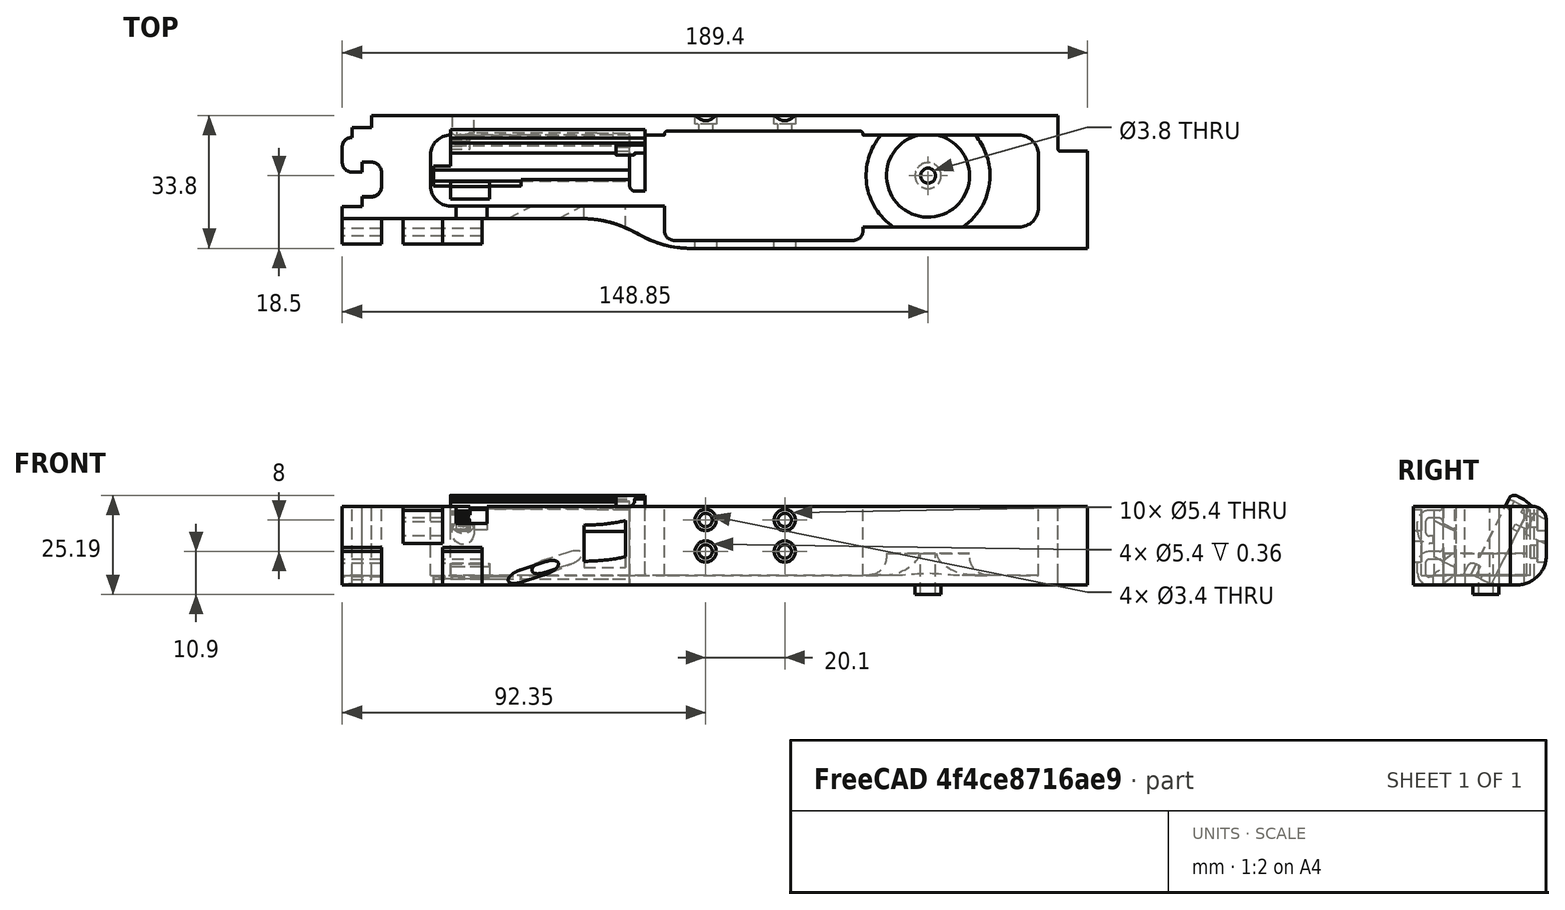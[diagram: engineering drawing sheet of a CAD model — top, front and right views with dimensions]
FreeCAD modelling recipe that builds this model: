
FCSTD DOCUMENT  (FreeCAD 0.19R0.19.2)
Label: v0_9991
License: All rights reserved
LicenseURL: http://en.wikipedia.org/wiki/All_rights_reserved
objects: Sketcher::SketchObject×44, Part::Extrusion×34, Part::MultiFuse×20, Part::Cut×15, Part::Box×14, Part::Fillet×11, App::MeasureDistance×5, Part::Cylinder×4, Part::Revolution×1, Mesh::Feature×1
note: 143 computed .brp shape members not serialized (recipe doc carries the construction recipe); baked Part::Feature solids carry a one-line shape summary decoded from their .brp

FEATURE [Sketcher::SketchObject] Sketch
  FullyConstrained = true
  sketch-geometry (36):
    g0: LineSegment StartX=0 StartY=0 StartZ=0 EndX=154.4 EndY=0 EndZ=0
    g1: LineSegment StartX=154.4 StartY=0 StartZ=0 EndX=154.4 EndY=-7.6 EndZ=0
    g2: LineSegment StartX=32.5209 StartY=-26.2 StartZ=0 EndX=-7.5 EndY=-26.2 EndZ=0
    g3-g7: Circle x5 (B-spline internal-alignment scaffolding for g8; pole/knot coordinates omitted)
    g8: BSplineCurve PolesCount=5 KnotsCount=3 Degree=3 IsPeriodic=0
    g9: GeomPoint X=61.85 Y=-33.8 Z=0
    g10: GeomPoint X=47.185 Y=-29.9 Z=0
    g11: GeomPoint X=32.5209 Y=-26.2 Z=0
    g12: Circle CenterX=121.35 CenterY=-14.3 CenterZ=0 NormalX=0 NormalY=0 NormalZ=1 AngleXU=0 Radius=3.25
    g13: LineSegment StartX=-7.5 StartY=-26.2 StartZ=0 EndX=-27.5 EndY=-26.2 EndZ=0
    g14: LineSegment StartX=-20 StartY=0 StartZ=0 EndX=0 EndY=0 EndZ=0
    g15: LineSegment StartX=-25 StartY=-3.1 StartZ=0 EndX=-20 EndY=-3.1 EndZ=0
    g16: LineSegment StartX=-25 StartY=-3.1 StartZ=0 EndX=-25 EndY=-5.6 EndZ=0
    g17: LineSegment StartX=-27.5 StartY=-8.1 StartZ=0 EndX=-27.5 EndY=-11.85 EndZ=0
    g18: ArcOfCircle CenterX=-25 CenterY=-8.1 CenterZ=0 NormalX=0 NormalY=0 NormalZ=1 AngleXU=0 Radius=2.5 StartAngle=1.5708 EndAngle=3.14159
    g19: LineSegment StartX=-25 StartY=-14.35 StartZ=0 EndX=-22.5 EndY=-14.35 EndZ=0
    g20: ArcOfCircle CenterX=-25 CenterY=-11.85 CenterZ=0 NormalX=0 NormalY=0 NormalZ=1 AngleXU=0 Radius=2.5 StartAngle=3.14159 EndAngle=4.71239
    g21: LineSegment StartX=-22.5 StartY=-14.35 StartZ=0 EndX=-22.5 EndY=-11.85 EndZ=0
    g22: LineSegment StartX=-22.5 StartY=-11.85 StartZ=0 EndX=-20 EndY=-11.85 EndZ=0
    g23: ArcOfCircle CenterX=-20 CenterY=-14.35 CenterZ=0 NormalX=0 NormalY=0 NormalZ=1 AngleXU=0 Radius=2.5 StartAngle=8e-16 EndAngle=1.5708
    g24: LineSegment StartX=-17.5 StartY=-14.35 StartZ=0 EndX=-17.5 EndY=-18.1 EndZ=0
    g25: ArcOfCircle CenterX=-20 CenterY=-18.1 CenterZ=0 NormalX=0 NormalY=0 NormalZ=1 AngleXU=0 Radius=2.5 StartAngle=4.71239 EndAngle=6.28319
    g26: LineSegment StartX=-22.5 StartY=-20.6 StartZ=0 EndX=-20 EndY=-20.6 EndZ=0
    g27: LineSegment StartX=-22.5 StartY=-20.6 StartZ=0 EndX=-22.5 EndY=-23.1 EndZ=0
    g28: LineSegment StartX=-27.5 StartY=-23.1 StartZ=0 EndX=-22.5 EndY=-23.1 EndZ=0
    g29: LineSegment StartX=-20 StartY=-3.1 StartZ=0 EndX=-20 EndY=0 EndZ=0
    g30: LineSegment StartX=-27.5 StartY=-23.1 StartZ=0 EndX=-27.5 EndY=-26.2 EndZ=0
    g31: LineSegment StartX=154.4 StartY=-7.6 StartZ=0 EndX=154.4 EndY=-8.6 EndZ=0
    g32: ArcOfCircle CenterX=154.9 CenterY=-8.6 CenterZ=0 NormalX=0 NormalY=0 NormalZ=1 AngleXU=0 Radius=0.5 StartAngle=3.14159 EndAngle=4.71239
    g33: LineSegment StartX=154.9 StartY=-9.1 StartZ=0 EndX=161.9 EndY=-9.1 EndZ=0
    g34: LineSegment StartX=161.9 StartY=-9.1 StartZ=0 EndX=161.9 EndY=-33.8 EndZ=0
    g35: LineSegment StartX=161.9 StartY=-33.8 StartZ=0 EndX=61.85 EndY=-33.8 EndZ=0
  constraints (72):
    c: PointOnObject(g0,g-2)
    c: Horizontal(g0)
    c: Distance(g0) = 154.4
    c: DistanceY(g-1,g0) = 0
    c: Vertical(g1)
    c: Distance(g1) = 7.6
    c: Coincident(g1,g0)
    c: Horizontal(g2)
    c: Block(g2)
    c: Weight(g3) = 1
    c: Coincident(g8,g2)
    c: InternalAlignment(g3-g7 -> g8) x5
    c: InternalAlignment(g9,g8)
    c: InternalAlignment(g10,g8)
    c: InternalAlignment(g11,g8)
    c: Block(g12)
    c: Coincident(g13,g2)
    c: Horizontal(g13)
    c: Distance(g13) = 20
    c: Horizontal(g14)
    c: Distance(g14) = 20
    c: Coincident(g14,g0)
    c: Horizontal(g15)
    c: Vertical(g16)
    c: Coincident(g16,g15)
    c: Vertical(g17)
    c: Coincident(g18,g16)
    c: Block(g18)
    c: Coincident(g17,g18)
    c: Horizontal(g19)
    c: Coincident(g20,g17)
    c: Block(g20)
    c: Block(g19)
    c: Vertical(g21)
    c: Coincident(g21,g19)
    c: Horizontal(g22)
    c: Coincident(g22,g21)
    c: Coincident(g23,g22)
    c: Vertical(g24)
    c: Block(g23)
    c: Coincident(g24,g23)
    c: Coincident(g25,g24)
    c: Block(g25)
    c: Horizontal(g26)
    c: Coincident(g26,g25)
    c: Vertical(g27)
    c: Coincident(g27,g26)
    c: Horizontal(g28)
    c: Coincident(g28,g27)
    c: Block(g15)
    c: Block(g28)
    c: Coincident(g29,g15)
    c: Coincident(g29,g14)
    c: Vertical(g29)
    c: Coincident(g30,g28)
    c: Coincident(g30,g13)
    c: Vertical(g30)
    c: Vertical(g31)
    c: Distance(g31) = 1
    c: Coincident(g31,g1)
    c: Coincident(g32,g31)
    c: Block(g32)
    c: Coincident(g33,g32)
    c: Horizontal(g33)
    c: Coincident(g34,g33)
    c: Vertical(g34)
    c: Block(g34)
    c: Coincident(g35,g34)
    c: Horizontal(g35)
    c: Block(g35)
    c: Coincident(g8,g35)
    c: Block(g8)
FEATURE [Part::Extrusion] Extrude  label="mainBodyBaseExtrude"
  Base = -> Sketch
  Dir = (0,0,1)
  DirMode = 2
  FaceMakerClass = Part::FaceMakerBullseye
  LengthFwd = 2.4
  LengthRev = 0
  Solid = true
  Symmetric = false
FEATURE [Sketcher::SketchObject] Sketch001
  FullyConstrained = true
  sketch-geometry (75):
    g0: ArcOfCircle CenterX=144.4 CenterY=-10 CenterZ=0 NormalX=0 NormalY=0 NormalZ=1 AngleXU=0 Radius=5 StartAngle=4.345e-13 EndAngle=1.5708
    g1: LineSegment StartX=32.5209 StartY=-26.2 StartZ=0 EndX=-7.49911 EndY=-26.2 EndZ=0
    g2: LineSegment StartX=0 StartY=0 StartZ=0 EndX=154.4 EndY=0 EndZ=0
    g3-g7: Circle x5 (B-spline internal-alignment scaffolding for g8; pole/knot coordinates omitted)
    g8: BSplineCurve PolesCount=5 KnotsCount=3 Degree=3 IsPeriodic=0
    g9: GeomPoint X=61.85 Y=-33.8 Z=0
    g10: GeomPoint X=47.1857 Y=-29.9 Z=0
    g11: GeomPoint X=32.5209 Y=-26.2 Z=0
    g12: LineSegment StartX=154.4 StartY=0 StartZ=0 EndX=154.4 EndY=-7.6 EndZ=0
    g13: LineSegment StartX=20 StartY=-5 StartZ=0 EndX=54.35 EndY=-5 EndZ=0
    g14: LineSegment StartX=104.85 StartY=-5 StartZ=0 EndX=144.4 EndY=-5 EndZ=0
    g15: LineSegment StartX=54.35 StartY=-23 StartZ=0 EndX=20 EndY=-23 EndZ=0
    g16: LineSegment StartX=-27.4991 StartY=-26.2 StartZ=0 EndX=-7.49911 EndY=-26.2 EndZ=0
    g17: LineSegment StartX=-20 StartY=0 StartZ=0 EndX=0 EndY=0 EndZ=0
    g18: LineSegment StartX=-27.4991 StartY=-23.2 StartZ=0 EndX=-22.5 EndY=-23.2 EndZ=0
    g19: LineSegment StartX=-22.5 StartY=-20.7 StartZ=0 EndX=-22.5 EndY=-23.2 EndZ=0
    g20: LineSegment StartX=-22.5 StartY=-20.7 StartZ=0 EndX=-20 EndY=-20.7 EndZ=0
    g21: ArcOfCircle CenterX=-20 CenterY=-18.2 CenterZ=0 NormalX=0 NormalY=0 NormalZ=1 AngleXU=0 Radius=2.5 StartAngle=4.71239 EndAngle=6.28319
    g22: LineSegment StartX=-17.5 StartY=-14.4 StartZ=0 EndX=-17.5 EndY=-18.2 EndZ=0
    g23: ArcOfCircle CenterX=-20 CenterY=-14.4 CenterZ=0 NormalX=0 NormalY=0 NormalZ=1 AngleXU=0 Radius=2.5 StartAngle=9e-16 EndAngle=1.5708
    g24: LineSegment StartX=-22.5 StartY=-11.9 StartZ=0 EndX=-20 EndY=-11.9 EndZ=0
    g25: LineSegment StartX=-22.5 StartY=-14.4 StartZ=0 EndX=-22.5 EndY=-11.9 EndZ=0
    g26: LineSegment StartX=-25 StartY=-14.4 StartZ=0 EndX=-22.5 EndY=-14.4 EndZ=0
    g27: ArcOfCircle CenterX=-25 CenterY=-11.9 CenterZ=0 NormalX=0 NormalY=0 NormalZ=1 AngleXU=0 Radius=2.5 StartAngle=3.14159 EndAngle=4.71239
    g28: LineSegment StartX=-27.5 StartY=-8.1 StartZ=0 EndX=-27.5 EndY=-11.9 EndZ=0
    g29: ArcOfCircle CenterX=-25 CenterY=-8.1 CenterZ=0 NormalX=0 NormalY=0 NormalZ=1 AngleXU=0 Radius=2.5 StartAngle=1.5708 EndAngle=3.14159
    g30: LineSegment StartX=-25 StartY=-3.1 StartZ=0 EndX=-25 EndY=-5.6 EndZ=0
    g31: LineSegment StartX=-20 StartY=-3.1 StartZ=0 EndX=-25 EndY=-3.1 EndZ=0
    g32: LineSegment StartX=-20 StartY=0 StartZ=0 EndX=-20 EndY=-3.1 EndZ=0
    g33: LineSegment StartX=-27.4991 StartY=-26.2 StartZ=0 EndX=-27.4991 EndY=-23.2 EndZ=0
    g34: LineSegment StartX=4.09e-14 StartY=-5 StartZ=0 EndX=20 EndY=-5 EndZ=0
    g35: ArcOfCircle CenterX=7.1e-15 CenterY=-18 CenterZ=0 NormalX=0 NormalY=0 NormalZ=1 AngleXU=0 Radius=5 StartAngle=3.14159 EndAngle=4.71239
    g36: ArcOfCircle CenterX=4.26e-14 CenterY=-10 CenterZ=0 NormalX=0 NormalY=0 NormalZ=1 AngleXU=0 Radius=5 StartAngle=1.5708 EndAngle=3.14159
    g37: LineSegment StartX=-5 StartY=-18 StartZ=0 EndX=-5 EndY=-10 EndZ=0
    g38: LineSegment StartX=6.2e-15 StartY=-23 StartZ=0 EndX=20 EndY=-23 EndZ=0
    g39: LineSegment StartX=154.4 StartY=-7.6 StartZ=0 EndX=154.4 EndY=-8.6 EndZ=0
    g40: LineSegment StartX=154.9 StartY=-9.1 StartZ=0 EndX=161.9 EndY=-9.1 EndZ=0
    g41: ArcOfCircle CenterX=154.9 CenterY=-8.6 CenterZ=0 NormalX=0 NormalY=0 NormalZ=1 AngleXU=0 Radius=0.5 StartAngle=3.14159 EndAngle=4.71299
    g42: LineSegment StartX=104.85 StartY=-28.3916 StartZ=0 EndX=144.408 EndY=-28.3916 EndZ=0
    g43: LineSegment StartX=149.4 StartY=-10 StartZ=0 EndX=149.4 EndY=-23.4 EndZ=0
    g44: ArcOfCircle CenterX=144.408 CenterY=-23.4 CenterZ=0 NormalX=0 NormalY=0 NormalZ=1 AngleXU=0 Radius=4.99164 StartAngle=4.71239 EndAngle=6.28319
    g45: LineSegment StartX=104.85 StartY=-28.3916 StartZ=0 EndX=104.85 EndY=-28.7833 EndZ=0
    g46: LineSegment StartX=54.35 StartY=-28.7916 StartZ=0 EndX=54.35 EndY=-23 EndZ=0
    g47: LineSegment StartX=161.9 StartY=-33.8 StartZ=0 EndX=161.9 EndY=-9.1 EndZ=0
    g48: LineSegment StartX=61.85 StartY=-33.8 StartZ=0 EndX=161.9 EndY=-33.8 EndZ=0
    g49: Circle CenterX=54.35 CenterY=-28.7916 CenterZ=0 NormalX=0 NormalY=0 NormalZ=1 AngleXU=0 Radius=1
    g50: Circle CenterX=54.35 CenterY=-31.7916 CenterZ=0 NormalX=0 NormalY=0 NormalZ=1 AngleXU=0 Radius=1
    g51: Circle CenterX=57.35 CenterY=-31.7916 CenterZ=0 NormalX=0 NormalY=0 NormalZ=1 AngleXU=0 Radius=1
    g52: BSplineCurve PolesCount=3 KnotsCount=2 Degree=2 IsPeriodic=0
    g53: GeomPoint X=54.35 Y=-28.7916 Z=0
    g54: GeomPoint X=57.35 Y=-31.7916 Z=0
    g55: Circle CenterX=104.85 CenterY=-28.7833 CenterZ=0 NormalX=0 NormalY=0 NormalZ=1 AngleXU=0 Radius=1
    g56: Circle CenterX=104.85 CenterY=-31.7916 CenterZ=0 NormalX=0 NormalY=0 NormalZ=1 AngleXU=0 Radius=1
    g57: Circle CenterX=101.85 CenterY=-31.7916 CenterZ=0 NormalX=0 NormalY=0 NormalZ=1 AngleXU=0 Radius=1
    g58: BSplineCurve PolesCount=3 KnotsCount=2 Degree=2 IsPeriodic=0
    g59: GeomPoint X=104.85 Y=-28.7833 Z=0
    g60: GeomPoint X=101.85 Y=-31.7916 Z=0
    g61: LineSegment StartX=57.35 StartY=-31.7916 StartZ=0 EndX=101.85 EndY=-31.7916 EndZ=0
    g62: Circle CenterX=54.35 CenterY=-5 CenterZ=0 NormalX=0 NormalY=0 NormalZ=1 AngleXU=0 Radius=1
    g63: Circle CenterX=54.35 CenterY=-4 CenterZ=0 NormalX=0 NormalY=0 NormalZ=1 AngleXU=0 Radius=1
    g64: Circle CenterX=55.15 CenterY=-4 CenterZ=0 NormalX=0 NormalY=0 NormalZ=1 AngleXU=0 Radius=1
    g65: BSplineCurve PolesCount=3 KnotsCount=2 Degree=2 IsPeriodic=0
    g66: GeomPoint X=54.35 Y=-5 Z=0
    g67: GeomPoint X=55.15 Y=-4 Z=0
    g68: Circle CenterX=104.85 CenterY=-5 CenterZ=0 NormalX=0 NormalY=0 NormalZ=1 AngleXU=0 Radius=1
    g69: Circle CenterX=104.85 CenterY=-4 CenterZ=0 NormalX=0 NormalY=0 NormalZ=1 AngleXU=0 Radius=1
    g70: Circle CenterX=104.05 CenterY=-4 CenterZ=0 NormalX=0 NormalY=0 NormalZ=1 AngleXU=0 Radius=1
    g71: BSplineCurve PolesCount=3 KnotsCount=2 Degree=2 IsPeriodic=0
    g72: GeomPoint X=104.85 Y=-5 Z=0
    g73: GeomPoint X=104.05 Y=-4 Z=0
    g74: LineSegment StartX=104.05 StartY=-4 StartZ=0 EndX=55.15 EndY=-4 EndZ=0
  constraints (156):
    c: PointOnObject(g2,g-2)
    c: DistanceY(g-1,g2) = 0
    c: Block(g0)
    c: Horizontal(g1)
    c: Distance(g1) = 40.02
    c: Horizontal(g2)
    c: Block(g2)
    c: Weight(g3) = 1
    c: Equal(g3, g4-g7) x4
    c: Coincident(g8,g1)
    c: InternalAlignment(g3-g7 -> g8) x5
    c: InternalAlignment(g9,g8)
    c: InternalAlignment(g10,g8)
    c: InternalAlignment(g11,g8)
    c: Vertical(g12)
    c: Coincident(g12,g2)
    c: Distance(g12) = 7.6
    c: Block(g12)
    c: Horizontal(g13)
    c: Coincident(g14,g0)
    c: Horizontal(g14)
    c: Horizontal(g15)
    c: Horizontal(g16)
    c: Distance(g16) = 20
    c: Coincident(g1,g16)
    c: Horizontal(g17)
    c: Distance(g17) = 20
    c: Coincident(g17,g2)
    c: Horizontal(g31)
    c: Vertical(g30)
    c: Coincident(g29,g30)
    c: Vertical(g28)
    c: Block(g29)
    c: Coincident(g27,g28)
    c: Block(g27)
    c: Horizontal(g26)
    c: Coincident(g26,g27)
    c: Vertical(g25)
    c: Coincident(g25,g26)
    c: Horizontal(g24)
    c: Coincident(g23,g24)
    c: Block(g23)
    c: Vertical(g22)
    c: Coincident(g21,g22)
    c: Block(g21)
    c: Horizontal(g20)
    c: Coincident(g20,g21)
    c: Vertical(g19)
    c: Coincident(g19,g20)
    c: Horizontal(g18)
    c: Coincident(g18,g19)
    c: Coincident(g32,g17)
    c: Coincident(g32,g31)
    c: Vertical(g32)
    c: Coincident(g33,g16)
    c: Coincident(g33,g18)
    c: Vertical(g33)
    c: Block(g33)
    c: Block(g18)
    c: Block(g22)
    c: Block(g26)
    c: Block(g25)
    c: Block(g24)
    c: Block(g28)
    c: Block(g31)
    c: Block(g30)
    c: Horizontal(g34)
    c: Distance(g34) = 20
    c: Block(g35)
    c: Block(g36)
    c: Coincident(g37,g35)
    c: Coincident(g37,g36)
    c: Vertical(g37)
    c: Coincident(g38,g35)
    c: Coincident(g38,g15)
    c: Horizontal(g38)
    c: Block(g38)
    c: Block(g34)
    c: Block(g13)
    c: Vertical(g39)
    c: Distance(g39) = 1
    c: Coincident(g39,g12)
    c: Horizontal(g40)
    c: Coincident(g41,g39)
    c: Coincident(g41,g40)
    c: Block(g39)
    c: Block(g41)
    c: Horizontal(g42)
    c: Vertical(g43)
    c: Distance(g43) = 13.4
    c: Coincident(g43,g0)
    c: Block(g42)
    c: Block(g43)
    c: Coincident(g44,g43)
    c: Coincident(g44,g42)
    c: Block(g44)
    c: Distance(g15) = 34.35
    c: Coincident(g45,g42)
    c: Vertical(g45)
    c: Coincident(g46,g15)
    c: Vertical(g46)
    c: Coincident(g47,g40)
    c: Vertical(g47)
    c: Block(g47)
    c: Coincident(g48,g47)
    c: Horizontal(g48)
    c: Block(g48)
    c: Coincident(g8,g48)
    c: Block(g8)
    c: Coincident(g52,g46)
    c: Weight(g49) = 1
    c: Equal(g49,g50)
    c: Equal(g49,g51)
    c: InternalAlignment(g49,g52)
    c: InternalAlignment(g50,g52)
    c: InternalAlignment(g51,g52)
    c: InternalAlignment(g53,g52)
    c: InternalAlignment(g54,g52)
    c: Coincident(g58,g45)
    c: Weight(g55) = 1
    c: Equal(g55,g56)
    c: Equal(g55,g57)
    c: InternalAlignment(g55,g58)
    c: InternalAlignment(g56,g58)
    c: InternalAlignment(g57,g58)
    c: InternalAlignment(g59,g58)
    c: InternalAlignment(g60,g58)
    c: Block(g58)
    c: Block(g52)
    c: Coincident(g61,g52)
    c: Coincident(g61,g58)
    c: Horizontal(g61)
    c: Block(g14)
    c: Coincident(g65,g13)
    c: Weight(g62) = 1
    c: Equal(g62,g63)
    c: Equal(g62,g64)
    c: InternalAlignment(g62,g65)
    c: InternalAlignment(g63,g65)
    c: InternalAlignment(g64,g65)
    c: InternalAlignment(g66,g65)
    c: InternalAlignment(g67,g65)
    c: Block(g65)
    c: Coincident(g71,g14)
    c: Weight(g68) = 1
    c: Equal(g68,g69)
    c: Equal(g68,g70)
    c: InternalAlignment(g68,g71)
    c: InternalAlignment(g69,g71)
    c: InternalAlignment(g70,g71)
    c: InternalAlignment(g72,g71)
    c: InternalAlignment(g73,g71)
    c: Block(g71)
    c: Coincident(g74,g71)
    c: Coincident(g74,g65)
    c: Horizontal(g74)
FEATURE [Sketcher::SketchObject] Sketch005
  FullyConstrained = true
  Placement = pos=(0,0,0) rot=(1,0,0;1.5708rad)
  sketch-geometry (4):
    g0: Circle CenterX=84.95 CenterY=16.5 CenterZ=0 NormalX=0 NormalY=0 NormalZ=1 AngleXU=0 Radius=1.7
    g1: Circle CenterX=84.95 CenterY=8.5 CenterZ=0 NormalX=0 NormalY=0 NormalZ=1 AngleXU=0 Radius=1.7
    g2: Circle CenterX=64.85 CenterY=8.5 CenterZ=0 NormalX=0 NormalY=0 NormalZ=1 AngleXU=0 Radius=1.7
    g3: Circle CenterX=64.85 CenterY=16.5 CenterZ=0 NormalX=0 NormalY=0 NormalZ=1 AngleXU=0 Radius=1.7
  constraints (4):
    c: Block(g0)
    c: Block(g1)
    c: Block(g2)
    c: Block(g3)
FEATURE [Part::Extrusion] Extrude004  label="removeFromMainBodyToCreateScrewHolesForSolenoidExtrude004"
  Base = -> Sketch005
  Dir = (0,-1,1.1e-15)
  DirMode = 2
  FaceMakerClass = Part::FaceMakerBullseye
  LengthFwd = 10
  LengthRev = 0
  Solid = true
  Symmetric = false
FEATURE [Sketcher::SketchObject] Sketch004
  FullyConstrained = true
  Placement = pos=(0,0,0) rot=(1,0,0;1.5708rad)
  sketch-geometry (12):
    g0: LineSegment StartX=15.75 StartY=2.5 StartZ=0 EndX=15.75 EndY=0 EndZ=0
    g1: Circle CenterX=15.75 CenterY=2.5 CenterZ=0 NormalX=0 NormalY=0 NormalZ=1 AngleXU=0 Radius=1
    g2: Circle CenterX=10.55 CenterY=2.5 CenterZ=0 NormalX=0 NormalY=0 NormalZ=1 AngleXU=0 Radius=1
    g3: Circle CenterX=10.55 CenterY=8 CenterZ=0 NormalX=0 NormalY=0 NormalZ=1 AngleXU=0 Radius=1
    g4: BSplineCurve PolesCount=3 KnotsCount=2 Degree=2 IsPeriodic=0
    g5: GeomPoint X=15.75 Y=2.5 Z=0
    g6: GeomPoint X=10.55 Y=8 Z=0
    g7: LineSegment StartX=1.9 StartY=8 StartZ=0 EndX=10.55 EndY=8 EndZ=0
    g8: LineSegment StartX=1.9 StartY=-2.4 StartZ=0 EndX=1.9 EndY=8 EndZ=0
    g9: LineSegment StartX=3.30092 StartY=-2.4 StartZ=0 EndX=3.30092 EndY=0 EndZ=0
    g10: LineSegment StartX=15.75 StartY=0 StartZ=0 EndX=3.30092 EndY=0 EndZ=0
    g11: LineSegment StartX=3.30092 StartY=-2.4 StartZ=0 EndX=1.9 EndY=-2.4 EndZ=0
  constraints (26):
    c: Vertical(g0)
    c: Distance(g0) = 2.5
    c: Coincident(g4,g0)
    c: Weight(g1) = 1
    c: Equal(g1,g2)
    c: Equal(g1,g3)
    c: InternalAlignment(g1,g4)
    c: InternalAlignment(g2,g4)
    c: InternalAlignment(g3,g4)
    c: InternalAlignment(g5,g4)
    c: InternalAlignment(g6,g4)
    c: Block(g4)
    c: Coincident(g7,g4)
    c: Horizontal(g7)
    c: Vertical(g8)
    c: Coincident(g8,g7)
    c: Block(g8)
    c: Vertical(g9)
    c: Coincident(g10,g0)
    c: PointOnObject(g10,g-1)
    c: Horizontal(g10)
    c: Coincident(g10,g9)
    c: Block(g9)
    c: Coincident(g11,g9)
    c: Coincident(g11,g8)
    c: Horizontal(g11)
FEATURE [Sketcher::SketchObject] Sketch007
  FullyConstrained = true
  Placement = pos=(0,-14.3,2.37) rot=(-1,0,0;2.03453rad)
  sketch-geometry (6):
    g0: LineSegment StartX=0 StartY=0 StartZ=0 EndX=45.5 EndY=0 EndZ=0
    g1: LineSegment StartX=0 StartY=0 StartZ=0 EndX=0 EndY=-21.2 EndZ=0
    g2: LineSegment StartX=45.5 StartY=0 StartZ=0 EndX=49.5 EndY=0 EndZ=0
    g3: LineSegment StartX=49.5 StartY=0 StartZ=0 EndX=49.5 EndY=-21.2 EndZ=0
    g4: LineSegment StartX=49.5 StartY=-21.2 StartZ=0 EndX=0 EndY=-21.2 EndZ=0
    g5: Circle CenterX=3.25 CenterY=-18.05 CenterZ=0 NormalX=0 NormalY=0 NormalZ=1 AngleXU=0 Radius=1.6
  constraints (15):
    c: Coincident(g0,g-1)
    c: Horizontal(g0)
    c: Distance(g0) = 45.5
    c: Coincident(g1,g0)
    c: Vertical(g1)
    c: Horizontal(g2)
    c: Distance(g2) = 4
    c: Coincident(g2,g0)
    c: Coincident(g3,g2)
    c: Vertical(g3)
    c: Block(g3)
    c: Coincident(g4,g3)
    c: Horizontal(g4)
    c: Coincident(g4,g1)
    c: Block(g5)
FEATURE [Part::Extrusion] Extrude005  label="solenoidDriverHolderExtrude005"
  Base = -> Sketch007
  Dir = (0,0.894389,-0.447291)
  DirMode = 2
  FaceMakerClass = Part::FaceMakerBullseye
  LengthFwd = 10
  LengthRev = 0
  Placement = pos=(0,0,-2) rot=(0,0,1;0rad)
  Solid = true
  Symmetric = false
FEATURE [Sketcher::SketchObject] Sketch008
  FullyConstrained = false
  Placement = pos=(0,-4.3,-2.6) rot=(-1,0,0;2.03453rad)
  sketch-geometry (1):
    g0: Circle CenterX=42.25 CenterY=-3.15 CenterZ=0 NormalX=0 NormalY=0 NormalZ=1 AngleXU=0 Radius=4.5
FEATURE [Sketcher::SketchObject] Sketch009
  FullyConstrained = true
  Placement = pos=(0,-4.3,-2.6) rot=(-1,0,0;2.03453rad)
  sketch-geometry (1):
    g0: Circle CenterX=3.25 CenterY=-18.0217 CenterZ=0 NormalX=0 NormalY=0 NormalZ=1 AngleXU=0 Radius=2.8
  constraints (1):
    c: Block(g0)
FEATURE [Sketcher::SketchObject] Sketch010
  FullyConstrained = true
  Placement = pos=(0,-14.3,2.37) rot=(-1,0,0;2.03453rad)
  sketch-geometry (1):
    g0: Circle CenterX=3.25 CenterY=-18.05 CenterZ=0 NormalX=0 NormalY=0 NormalZ=1 AngleXU=0 Radius=1.6
  constraints (1):
    c: Block(g0)
FEATURE [Part::Extrusion] Extrude008  label="removeFromScrewHole3"
  Base = -> Sketch010
  Dir = (0,0.894389,-0.447291)
  DirMode = 2
  FaceMakerClass = Part::FaceMakerBullseye
  LengthFwd = -25
  LengthRev = 0
  Placement = pos=(0,4,-4) rot=(0,0,1;0rad)
  Solid = true
  Symmetric = false
FEATURE [Sketcher::SketchObject] Sketch011
  FullyConstrained = true
  Placement = pos=(0,-14.3,2.37) rot=(-1,0,0;2.03453rad)
  sketch-geometry (4):
    g0: LineSegment StartX=49.5 StartY=-21.2 StartZ=0 EndX=49.5 EndY=-22.8 EndZ=0
    g1: LineSegment StartX=49.5 StartY=-22.8 StartZ=0 EndX=0.002238 EndY=-22.8 EndZ=0
    g2: LineSegment StartX=0.002238 StartY=-21.2 StartZ=0 EndX=0.002238 EndY=-22.8 EndZ=0
    g3: LineSegment StartX=49.5 StartY=-21.2 StartZ=0 EndX=0.002238 EndY=-21.2 EndZ=0
  constraints (10):
    c: Vertical(g0)
    c: Distance(g0) = 1.6
    c: Coincident(g1,g0)
    c: Horizontal(g1)
    c: Vertical(g2)
    c: Coincident(g2,g1)
    c: Coincident(g3,g0)
    c: Coincident(g3,g2)
    c: Horizontal(g3)
    c: Block(g3)
FEATURE [Part::Extrusion] Extrude009  label="solenoidDriverTopLipFront"
  Base = -> Sketch011
  Dir = (0,0.894389,-0.447291)
  DirMode = 2
  FaceMakerClass = Part::FaceMakerBullseye
  LengthFwd = -2
  LengthRev = 0
  Placement = pos=(0,-2.9,-0.35) rot=(0,0,1;0rad)
  Solid = true
  Symmetric = false
FEATURE [Sketcher::SketchObject] Sketch012
  FullyConstrained = true
  Placement = pos=(0,-14.3,2.37) rot=(-1,0,0;2.03453rad)
  sketch-geometry (4):
    g0: LineSegment StartX=49.5 StartY=-21.2 StartZ=0 EndX=49.5 EndY=-22.8 EndZ=0
    g1: LineSegment StartX=49.5 StartY=-22.8 StartZ=0 EndX=0.002238 EndY=-22.8 EndZ=0
    g2: LineSegment StartX=0.002238 StartY=-21.2 StartZ=0 EndX=0.002238 EndY=-22.8 EndZ=0
    g3: LineSegment StartX=49.5 StartY=-21.2 StartZ=0 EndX=0.002238 EndY=-21.2 EndZ=0
  constraints (10):
    c: Vertical(g0)
    c: Distance(g0) = 1.6
    c: Coincident(g1,g0)
    c: Horizontal(g1)
    c: Vertical(g2)
    c: Coincident(g2,g1)
    c: Coincident(g3,g0)
    c: Coincident(g3,g2)
    c: Horizontal(g3)
    c: Block(g3)
FEATURE [Part::Extrusion] Extrude010  label="solenoidDriverTopLipLowerExtrude010"
  Base = -> Sketch012
  Dir = (0,0.894389,-0.447291)
  DirMode = 2
  FaceMakerClass = Part::FaceMakerBullseye
  LengthFwd = 5.05
  LengthRev = 0
  Solid = true
  Symmetric = false
FEATURE [Sketcher::SketchObject] Sketch015
  FullyConstrained = true
  Placement = pos=(0,-14.3,2.37) rot=(-1,0,0;2.03453rad)
  sketch-geometry (4):
    g0: LineSegment StartX=0 StartY=1.5 StartZ=0 EndX=0 EndY=0 EndZ=0
    g1: LineSegment StartX=0 StartY=1.5 StartZ=0 EndX=5 EndY=1.5 EndZ=0
    g2: LineSegment StartX=5 StartY=1.5 StartZ=0 EndX=5 EndY=0 EndZ=0
    g3: LineSegment StartX=0 StartY=0 StartZ=0 EndX=5 EndY=0 EndZ=0
  constraints (13):
    c: Vertical(g0)
    c: Distance(g0) = 1.5
    c: Horizontal(g1)
    c: Distance(g1) = 5
    c: Coincident(g1,g0)
    c: Vertical(g2)
    c: Distance(g2) = 1.5
    c: Coincident(g2,g1)
    c: Block(g1)
    c: Block(g2)
    c: Block(g0)
    c: Coincident(g3,g0)
    c: Coincident(g3,g2)
FEATURE [Part::Extrusion] Extrude013  label="solenoidDriverBottomLipTopExtrude012"
  Base = -> Sketch015
  Dir = (0,0.894389,-0.447291)
  DirMode = 2
  FaceMakerClass = Part::FaceMakerBullseye
  LengthFwd = -6.5
  LengthRev = 0
  Placement = pos=(0,-14.15,19.65) rot=(1,0,0;1.5708rad)
  Solid = true
  Symmetric = false
FEATURE [Sketcher::SketchObject] Sketch016
  FullyConstrained = true
  Placement = pos=(0,0,0) rot=(1,0,0;1.5708rad)
  sketch-geometry (4):
    g0: Circle CenterX=84.15 CenterY=16.5 CenterZ=0 NormalX=0 NormalY=0 NormalZ=1 AngleXU=0 Radius=2.7
    g1: Circle CenterX=64.05 CenterY=16.5 CenterZ=0 NormalX=0 NormalY=0 NormalZ=1 AngleXU=0 Radius=2.7
    g2: Circle CenterX=64.05 CenterY=8.5 CenterZ=0 NormalX=0 NormalY=0 NormalZ=1 AngleXU=0 Radius=2.7
    g3: Circle CenterX=84.15 CenterY=8.5 CenterZ=0 NormalX=0 NormalY=0 NormalZ=1 AngleXU=0 Radius=2.7
  constraints (4):
    c: Block(g0)
    c: Block(g1)
    c: Block(g3)
    c: Block(g2)
FEATURE [Part::Extrusion] Extrude014  label="removeFromMainBodyToCreateScrewHoleCounterSinks"
  Base = -> Sketch016
  Dir = (0,-1,1.1e-15)
  DirMode = 2
  FaceMakerClass = Part::FaceMakerBullseye
  LengthFwd = 1.9
  LengthRev = 0
  Placement = pos=(0.8,-0.36,0) rot=(0,0,1;0rad)
  Solid = true
  Symmetric = false
FEATURE [Part::Extrusion] Extrude015  label="removeFromScrewHole2Extrude007"
  Base = -> Sketch009
  Dir = (0,0.894389,-0.447291)
  DirMode = 2
  FaceMakerClass = Part::FaceMakerBullseye
  LengthFwd = 10
  LengthRev = 0
  Placement = pos=(0,-8,2) rot=(0,0,1;0rad)
  Solid = true
  Symmetric = false
FEATURE [Sketcher::SketchObject] Sketch017
  FullyConstrained = true
  Placement = pos=(0,-14.3,2.37) rot=(-1,0,0;2.03453rad)
  sketch-geometry (4):
    g0: LineSegment StartX=0 StartY=1.5 StartZ=0 EndX=0 EndY=0 EndZ=0
    g1: LineSegment StartX=0 StartY=1.5 StartZ=0 EndX=5 EndY=1.5 EndZ=0
    g2: LineSegment StartX=5 StartY=1.5 StartZ=0 EndX=5 EndY=0 EndZ=0
    g3: LineSegment StartX=0 StartY=0 StartZ=0 EndX=5 EndY=0 EndZ=0
  constraints (13):
    c: Vertical(g0)
    c: Distance(g0) = 1.5
    c: Horizontal(g1)
    c: Distance(g1) = 5
    c: Coincident(g1,g0)
    c: Vertical(g2)
    c: Distance(g2) = 1.5
    c: Coincident(g2,g1)
    c: Block(g1)
    c: Block(g2)
    c: Block(g0)
    c: Coincident(g3,g0)
    c: Coincident(g3,g2)
FEATURE [Part::Extrusion] Extrude016  label="solenoidDriverBottomLipTopExtrude013"
  Base = -> Sketch017
  Dir = (0,0.894389,-0.447291)
  DirMode = 2
  FaceMakerClass = Part::FaceMakerBullseye
  LengthFwd = -6.5
  LengthRev = 0
  Placement = pos=(0,-15.45,20.3) rot=(1,0,0;1.5708rad)
  Solid = true
  Symmetric = false
FEATURE [Part::Fillet] Fillet005  label="solenoidDriverBottomLipTopFillet005"
  Base = -> Extrude016
  Edges = 1 edges r=1.4: [Edge6]
FEATURE [Sketcher::SketchObject] Sketch018
  FullyConstrained = true
  Placement = pos=(38.5,-14.3,2.37) rot=(-1,0,0;2.03453rad)
  sketch-geometry (4):
    g0: LineSegment StartX=11 StartY=0 StartZ=0 EndX=11 EndY=1.5 EndZ=0
    g1: LineSegment StartX=11 StartY=0 StartZ=0 EndX=3.6 EndY=0 EndZ=0
    g2: LineSegment StartX=3.6 StartY=0 StartZ=0 EndX=3.6 EndY=1.5 EndZ=0
    g3: LineSegment StartX=11 StartY=1.5 StartZ=0 EndX=3.6 EndY=1.5 EndZ=0
  constraints (12):
    c: PointOnObject(g0,g-1)
    c: Vertical(g0)
    c: Distance(g0) = 1.5
    c: Horizontal(g1)
    c: Distance(g1) = 7.4
    c: Coincident(g1,g0)
    c: Block(g0)
    c: Coincident(g2,g1)
    c: Vertical(g2)
    c: Coincident(g3,g0)
    c: Horizontal(g3)
    c: Coincident(g2,g3)
FEATURE [Part::Extrusion] Extrude017
  Base = -> Sketch018
  Dir = (0,0.894389,-0.447291)
  DirMode = 2
  FaceMakerClass = Part::FaceMakerBullseye
  LengthFwd = 4
  LengthRev = 0
  Placement = pos=(0,-8.212,34.025) rot=(1,0,0;1.5708rad)
  Solid = true
  Symmetric = false
FEATURE [Sketcher::SketchObject] Sketch019
  FullyConstrained = true
  Placement = pos=(0,0,0) rot=(1,0,0;1.5708rad)
  sketch-geometry (4):
    g0: Circle CenterX=84.95 CenterY=8.5 CenterZ=0 NormalX=0 NormalY=0 NormalZ=1 AngleXU=0 Radius=2.7
    g1: Circle CenterX=64.85 CenterY=8.5 CenterZ=0 NormalX=0 NormalY=0 NormalZ=1 AngleXU=0 Radius=2.7
    g2: Circle CenterX=64.85 CenterY=16.5 CenterZ=0 NormalX=0 NormalY=0 NormalZ=1 AngleXU=0 Radius=2.7
    g3: Circle CenterX=84.95 CenterY=16.5 CenterZ=0 NormalX=0 NormalY=0 NormalZ=1 AngleXU=0 Radius=2.7
  constraints (4):
    c: Block(g3)
    c: Block(g2)
    c: Block(g0)
    c: Block(g1)
FEATURE [Part::Extrusion] Extrude019  label="removeSolenoidAdjusterHoles"
  Base = -> Sketch019
  Dir = (0,-1,1.1e-15)
  DirMode = 2
  FaceMakerClass = Part::FaceMakerBullseye
  LengthFwd = 6
  LengthRev = 0
  Placement = pos=(0,-30,0) rot=(0,0,1;0rad)
  Solid = true
  Symmetric = false
FEATURE [Sketcher::SketchObject] Sketch020
  FullyConstrained = true
  Placement = pos=(0,-14.3,2.37) rot=(-1,0,0;2.03453rad)
  sketch-geometry (6):
    g0: LineSegment StartX=45.5 StartY=-21.2 StartZ=0 EndX=49.5 EndY=-21.2 EndZ=0
    g1: LineSegment StartX=45.5 StartY=0 StartZ=0 EndX=49.5 EndY=0 EndZ=0
    g2: LineSegment StartX=49.5 StartY=0 StartZ=0 EndX=49.5 EndY=-21.2 EndZ=0
    g3: LineSegment StartX=4 StartY=0 StartZ=0 EndX=4 EndY=-21.2 EndZ=0
    g4: LineSegment StartX=45.5 StartY=-21.2 StartZ=0 EndX=4 EndY=-21.2 EndZ=0
    g5: LineSegment StartX=4 StartY=0 StartZ=0 EndX=45.5 EndY=0 EndZ=0
  constraints (16):
    c: Horizontal(g0)
    c: Distance(g0) = 4
    c: Horizontal(g1)
    c: Distance(g1) = 4
    c: Coincident(g2,g1)
    c: Coincident(g2,g0)
    c: Vertical(g2)
    c: Block(g2)
    c: Vertical(g3)
    c: Coincident(g4,g0)
    c: Horizontal(g4)
    c: Coincident(g4,g3)
    c: Coincident(g5,g1)
    c: Horizontal(g5)
    c: Block(g3)
    c: Block(g5)
FEATURE [Part::Box] Box  label="Cube"
  AttacherType = Attacher::AttachEngine3D
  Height = 10
  Length = 190
  Placement = pos=(-30,0,0) rot=(0,0,1;0rad)
  Width = 10
FEATURE [Part::Fillet] Fillet008
  Base = -> Box
  Edges = 1 edges r=7.5: [Edge11]
FEATURE [Part::Box] Box001  label="Cube001"
  AttacherType = Attacher::AttachEngine3D
  Height = 10
  Length = 190
  Placement = pos=(-35,0,0) rot=(0,0,1;0rad)
  Width = 10
FEATURE [Part::Cut] Cut  label="filletMain"
  Base = -> Box001
  Placement = pos=(0,-10,0) rot=(0,0,1;0rad)
  Tool = -> Fillet008
FEATURE [Part::Box] Box002  label="Cube002"
  AttacherType = Attacher::AttachEngine3D
  Height = 30
  Length = 190
  Placement = pos=(-20,0,0) rot=(0,0,1;0rad)
  Width = 10
FEATURE [Part::Box] Box003  label="Cube003"
  AttacherType = Attacher::AttachEngine3D
  Height = 10
  Length = 190
  Placement = pos=(-90,-50,-10) rot=(0,0,1;0rad)
  Width = 50
FEATURE [Sketcher::SketchObject] Sketch021
  FullyConstrained = true
  Placement = pos=(0,-14.3,2.37) rot=(-1,0,0;2.03453rad)
  sketch-geometry (6):
    g0: LineSegment StartX=41.65 StartY=-3.15 StartZ=0 EndX=38.95 EndY=-3.15 EndZ=0
    g1: LineSegment StartX=36.25 StartY=-3.15 StartZ=0 EndX=38.95 EndY=-3.15 EndZ=0
    g2: LineSegment StartX=41.65 StartY=-3.15 StartZ=0 EndX=41.65 EndY=-7.15 EndZ=0
    g3: LineSegment StartX=38.95 StartY=-7.15 StartZ=0 EndX=41.65 EndY=-7.15 EndZ=0
    g4: LineSegment StartX=38.95 StartY=-7.15 StartZ=0 EndX=36.25 EndY=-7.15 EndZ=0
    g5: LineSegment StartX=36.25 StartY=-3.15 StartZ=0 EndX=36.25 EndY=-7.15 EndZ=0
  constraints (16):
    c: Horizontal(g0)
    c: Distance(g0) = 2.7
    c: Horizontal(g1)
    c: Distance(g1) = 2.7
    c: Coincident(g1,g0)
    c: Block(g0)
    c: Coincident(g2,g0)
    c: Vertical(g2)
    c: Horizontal(g3)
    c: Coincident(g3,g2)
    c: Horizontal(g4)
    c: Coincident(g5,g1)
    c: Vertical(g5)
    c: Coincident(g5,g4)
    c: Block(g3)
    c: Block(g4)
FEATURE [Sketcher::SketchObject] Sketch022
  FullyConstrained = true
  Placement = pos=(0,-14.3,2.37) rot=(-1,0,0;2.03453rad)
  sketch-geometry (6):
    g0: LineSegment StartX=41.65 StartY=-3.15 StartZ=0 EndX=38.95 EndY=-3.15 EndZ=0
    g1: LineSegment StartX=36.25 StartY=-3.15 StartZ=0 EndX=38.95 EndY=-3.15 EndZ=0
    g2: LineSegment StartX=41.65 StartY=-3.15 StartZ=0 EndX=41.65 EndY=-7.15 EndZ=0
    g3: LineSegment StartX=38.95 StartY=-7.15 StartZ=0 EndX=41.65 EndY=-7.15 EndZ=0
    g4: LineSegment StartX=38.95 StartY=-7.15 StartZ=0 EndX=36.25 EndY=-7.15 EndZ=0
    g5: LineSegment StartX=36.25 StartY=-3.15 StartZ=0 EndX=36.25 EndY=-7.15 EndZ=0
  constraints (16):
    c: Horizontal(g0)
    c: Distance(g0) = 2.7
    c: Horizontal(g1)
    c: Distance(g1) = 2.7
    c: Coincident(g1,g0)
    c: Block(g0)
    c: Coincident(g2,g0)
    c: Vertical(g2)
    c: Horizontal(g3)
    c: Coincident(g3,g2)
    c: Horizontal(g4)
    c: Coincident(g5,g1)
    c: Vertical(g5)
    c: Coincident(g5,g4)
    c: Block(g3)
    c: Block(g4)
FEATURE [Sketcher::SketchObject] Sketch024
  FullyConstrained = true
  Placement = pos=(0,-14.3,2.37) rot=(-1,0,0;2.03453rad)
  sketch-geometry (4):
    g0: LineSegment StartX=49.5 StartY=-21.2 StartZ=0 EndX=49.5 EndY=-22.8 EndZ=0
    g1: LineSegment StartX=49.5 StartY=-22.8 StartZ=0 EndX=0.002238 EndY=-22.8 EndZ=0
    g2: LineSegment StartX=0.002238 StartY=-21.2 StartZ=0 EndX=0.002238 EndY=-22.8 EndZ=0
    g3: LineSegment StartX=49.5 StartY=-21.2 StartZ=0 EndX=0.002238 EndY=-21.2 EndZ=0
  constraints (10):
    c: Vertical(g0)
    c: Distance(g0) = 1.6
    c: Coincident(g1,g0)
    c: Horizontal(g1)
    c: Vertical(g2)
    c: Coincident(g2,g1)
    c: Coincident(g3,g0)
    c: Coincident(g3,g2)
    c: Horizontal(g3)
    c: Block(g3)
FEATURE [Sketcher::SketchObject] Sketch025
  FullyConstrained = true
  Placement = pos=(0,-14.3,2.37) rot=(-1,0,0;2.03453rad)
  sketch-geometry (4):
    g0: LineSegment StartX=0 StartY=1.5 StartZ=0 EndX=0 EndY=0 EndZ=0
    g1: LineSegment StartX=0 StartY=1.5 StartZ=0 EndX=5 EndY=1.5 EndZ=0
    g2: LineSegment StartX=5 StartY=1.5 StartZ=0 EndX=5 EndY=0 EndZ=0
    g3: LineSegment StartX=0 StartY=0 StartZ=0 EndX=5 EndY=0 EndZ=0
  constraints (13):
    c: Vertical(g0)
    c: Distance(g0) = 1.5
    c: Horizontal(g1)
    c: Distance(g1) = 5
    c: Coincident(g1,g0)
    c: Vertical(g2)
    c: Distance(g2) = 1.5
    c: Coincident(g2,g1)
    c: Block(g1)
    c: Block(g2)
    c: Block(g0)
    c: Coincident(g3,g0)
    c: Coincident(g3,g2)
FEATURE [Part::Extrusion] Extrude022  label="solenoidDriverBottomLipTopExtrude014"
  Base = -> Sketch025
  Dir = (0,0.894389,-0.447291)
  DirMode = 2
  FaceMakerClass = Part::FaceMakerBullseye
  LengthFwd = -6.5
  LengthRev = 0
  Placement = pos=(0,-15.45,20.3) rot=(1,0,0;1.5708rad)
  Solid = true
  Symmetric = false
FEATURE [Part::Fillet] Fillet013  label="solenoidDriverBottomLipTopFillet006"
  Base = -> Extrude022
  Edges = 1 edges r=1.4: [Edge6]
  Placement = pos=(5,0,0) rot=(0,0,1;0rad)
FEATURE [Sketcher::SketchObject] Sketch026
  FullyConstrained = true
  Placement = pos=(0,-14.3,2.37) rot=(-1,0,0;2.03453rad)
  sketch-geometry (4):
    g0: LineSegment StartX=0 StartY=1.5 StartZ=0 EndX=0 EndY=0 EndZ=0
    g1: LineSegment StartX=0 StartY=1.5 StartZ=0 EndX=5 EndY=1.5 EndZ=0
    g2: LineSegment StartX=5 StartY=1.5 StartZ=0 EndX=5 EndY=0 EndZ=0
    g3: LineSegment StartX=0 StartY=0 StartZ=0 EndX=5 EndY=0 EndZ=0
  constraints (13):
    c: Vertical(g0)
    c: Distance(g0) = 1.5
    c: Horizontal(g1)
    c: Distance(g1) = 5
    c: Coincident(g1,g0)
    c: Vertical(g2)
    c: Distance(g2) = 1.5
    c: Coincident(g2,g1)
    c: Block(g1)
    c: Block(g2)
    c: Block(g0)
    c: Coincident(g3,g0)
    c: Coincident(g3,g2)
FEATURE [Part::Extrusion] Extrude023  label="solenoidDriverBottomLipTopExtrude015"
  Base = -> Sketch026
  Dir = (0,0.894389,-0.447291)
  DirMode = 2
  FaceMakerClass = Part::FaceMakerBullseye
  LengthFwd = -6.5
  LengthRev = 0
  Placement = pos=(5,-14.15,19.65) rot=(1,0,0;1.5708rad)
  Solid = true
  Symmetric = false
FEATURE [Sketcher::SketchObject] Sketch027
  FullyConstrained = true
  Placement = pos=(0,-14.3,2.37) rot=(-1,0,0;2.03453rad)
  sketch-geometry (5):
    g0: LineSegment StartX=45.5 StartY=-21.2 StartZ=0 EndX=49.5 EndY=-21.2 EndZ=0
    g1: LineSegment StartX=49.5 StartY=0 StartZ=0 EndX=49.5 EndY=-21.2 EndZ=0
    g2: LineSegment StartX=49.5 StartY=0 StartZ=0 EndX=49.5 EndY=1.6 EndZ=0
    g3: LineSegment StartX=45.5 StartY=-21.2 StartZ=0 EndX=45.5 EndY=1.6 EndZ=0
    g4: LineSegment StartX=49.5 StartY=1.6 StartZ=0 EndX=45.5 EndY=1.6 EndZ=0
  constraints (14):
    c: Horizontal(g0)
    c: Distance(g0) = 4
    c: Coincident(g1,g0)
    c: Vertical(g1)
    c: Block(g1)
    c: Vertical(g2)
    c: Distance(g2) = 1.6
    c: Block(g2)
    c: Coincident(g3,g0)
    c: Vertical(g3)
    c: Coincident(g4,g2)
    c: Horizontal(g4)
    c: Block(g0)
    c: Coincident(g3,g4)
FEATURE [Part::Extrusion] Extrude024
  Base = -> Sketch027
  Dir = (0,0.894389,-0.447291)
  DirMode = 2
  FaceMakerClass = Part::FaceMakerBullseye
  LengthFwd = 6.34
  LengthRev = 0
  Placement = pos=(0,-5.59,1) rot=(0,0,1;0rad)
  Solid = true
  Symmetric = false
FEATURE [Part::Fillet] Fillet014  label="solenoidDriverSideBarFillet014"
  Base = -> Extrude024
  Edges = 1 edges r=1.4: [Edge14]
  Placement = pos=(0,0.9,-0.45) rot=(0,0,1;0rad)
FEATURE [Part::Revolution] Revolve  label="mainScrewStandRevolve"
  Angle = 360
  Axis = (0,0,1)
  Base = (0,0,0)
  FaceMakerClass = Part::FaceMakerBullseye
  Placement = pos=(121.35,-15.3,0) rot=(0,0,1;0rad)
  Solid = true
  Source = -> Sketch004
  Symmetric = false
FEATURE [Part::Extrusion] Extrude021  label="solenoidDriverTopLipLowerExtrude011"
  Base = -> Sketch024
  Dir = (0,0.894389,-0.447291)
  DirMode = 2
  FaceMakerClass = Part::FaceMakerBullseye
  LengthFwd = 5.05
  LengthRev = 0
  Solid = true
  Symmetric = false
FEATURE [Part::Fillet] Fillet012  label="solenoidDriverTopLipLowerFillet004"
  Base = -> Extrude021
  Edges = 1 edges r=1.2: [Edge7]
  Placement = pos=(0,-0.9,-1.35) rot=(0,0,1;0rad)
FEATURE [Part::Fillet] Fillet003  label="solenoidDriverTopLipLowerFillet003"
  Base = -> Extrude010
  Edges = 1 edges r=1.2: [Edge7]
  Placement = pos=(0,-3,-0.3) rot=(0,0,1;0rad)
FEATURE [Part::Extrusion] Extrude025  label="mainBodyUpperExtrude025"
  Base = -> Sketch001
  Dir = (0,0,1)
  DirMode = 2
  FaceMakerClass = Part::FaceMakerBullseye
  LengthFwd = 20
  LengthRev = 0
  Solid = true
  Symmetric = false
FEATURE [Part::MultiFuse] Fusion  label="solenoidDriverBottomLipFusion"
  Placement = pos=(0,-1.6,0) rot=(0,0,1;0rad)
  Shapes = -> [Fillet005,Fillet013,Extrude023,Extrude013]
FEATURE [Sketcher::SketchObject] Sketch028
  FullyConstrained = true
  Placement = pos=(0,-14.3,2.37) rot=(-1,0,0;2.03453rad)
  sketch-geometry (4):
    g0: LineSegment StartX=0 StartY=1.5 StartZ=0 EndX=0 EndY=0 EndZ=0
    g1: LineSegment StartX=0 StartY=1.5 StartZ=0 EndX=5 EndY=1.5 EndZ=0
    g2: LineSegment StartX=5 StartY=1.5 StartZ=0 EndX=5 EndY=0 EndZ=0
    g3: LineSegment StartX=0 StartY=0 StartZ=0 EndX=5 EndY=0 EndZ=0
  constraints (13):
    c: Vertical(g0)
    c: Distance(g0) = 1.5
    c: Horizontal(g1)
    c: Distance(g1) = 5
    c: Coincident(g1,g0)
    c: Vertical(g2)
    c: Distance(g2) = 1.5
    c: Coincident(g2,g1)
    c: Block(g1)
    c: Block(g2)
    c: Block(g0)
    c: Coincident(g3,g0)
    c: Coincident(g3,g2)
FEATURE [Part::Extrusion] Extrude026  label="solenoidDriverBottomLipTopExtrude016"
  Base = -> Sketch028
  Dir = (0,0.894389,-0.447291)
  DirMode = 2
  FaceMakerClass = Part::FaceMakerBullseye
  LengthFwd = -6.5
  LengthRev = 0
  Placement = pos=(5,-14.15,19.65) rot=(1,0,0;1.5708rad)
  Solid = true
  Symmetric = false
FEATURE [Sketcher::SketchObject] Sketch029
  FullyConstrained = true
  Placement = pos=(0,-14.3,2.37) rot=(-1,0,0;2.03453rad)
  sketch-geometry (4):
    g0: LineSegment StartX=0 StartY=1.5 StartZ=0 EndX=0 EndY=0 EndZ=0
    g1: LineSegment StartX=0 StartY=1.5 StartZ=0 EndX=5 EndY=1.5 EndZ=0
    g2: LineSegment StartX=5 StartY=1.5 StartZ=0 EndX=5 EndY=0 EndZ=0
    g3: LineSegment StartX=0 StartY=0 StartZ=0 EndX=5 EndY=0 EndZ=0
  constraints (13):
    c: Vertical(g0)
    c: Distance(g0) = 1.5
    c: Horizontal(g1)
    c: Distance(g1) = 5
    c: Coincident(g1,g0)
    c: Vertical(g2)
    c: Distance(g2) = 1.5
    c: Coincident(g2,g1)
    c: Block(g1)
    c: Block(g2)
    c: Block(g0)
    c: Coincident(g3,g0)
    c: Coincident(g3,g2)
FEATURE [Part::Extrusion] Extrude027  label="solenoidDriverBottomLipTopExtrude017"
  Base = -> Sketch029
  Dir = (0,0.894389,-0.447291)
  DirMode = 2
  FaceMakerClass = Part::FaceMakerBullseye
  LengthFwd = -6.5
  LengthRev = 0
  Placement = pos=(0,-14.15,19.65) rot=(1,0,0;1.5708rad)
  Solid = true
  Symmetric = false
FEATURE [Sketcher::SketchObject] Sketch030
  FullyConstrained = true
  Placement = pos=(0,-14.3,2.37) rot=(-1,0,0;2.03453rad)
  sketch-geometry (4):
    g0: LineSegment StartX=0 StartY=1.5 StartZ=0 EndX=0 EndY=0 EndZ=0
    g1: LineSegment StartX=0 StartY=1.5 StartZ=0 EndX=5 EndY=1.5 EndZ=0
    g2: LineSegment StartX=5 StartY=1.5 StartZ=0 EndX=5 EndY=0 EndZ=0
    g3: LineSegment StartX=0 StartY=0 StartZ=0 EndX=5 EndY=0 EndZ=0
  constraints (13):
    c: Vertical(g0)
    c: Distance(g0) = 1.5
    c: Horizontal(g1)
    c: Distance(g1) = 5
    c: Coincident(g1,g0)
    c: Vertical(g2)
    c: Distance(g2) = 1.5
    c: Coincident(g2,g1)
    c: Block(g1)
    c: Block(g2)
    c: Block(g0)
    c: Coincident(g3,g0)
    c: Coincident(g3,g2)
FEATURE [Sketcher::SketchObject] Sketch031
  FullyConstrained = true
  Placement = pos=(0,-14.3,2.37) rot=(-1,0,0;2.03453rad)
  sketch-geometry (6):
    g0: LineSegment StartX=45.5 StartY=-21.2 StartZ=0 EndX=49.5 EndY=-21.2 EndZ=0
    g1: LineSegment StartX=45.5 StartY=0 StartZ=0 EndX=49.5 EndY=0 EndZ=0
    g2: LineSegment StartX=49.5 StartY=0 StartZ=0 EndX=49.5 EndY=-21.2 EndZ=0
    g3: LineSegment StartX=4 StartY=0 StartZ=0 EndX=4 EndY=-21.2 EndZ=0
    g4: LineSegment StartX=45.5 StartY=-21.2 StartZ=0 EndX=4 EndY=-21.2 EndZ=0
    g5: LineSegment StartX=4 StartY=0 StartZ=0 EndX=45.5 EndY=0 EndZ=0
  constraints (16):
    c: Horizontal(g0)
    c: Distance(g0) = 4
    c: Horizontal(g1)
    c: Distance(g1) = 4
    c: Coincident(g2,g1)
    c: Coincident(g2,g0)
    c: Vertical(g2)
    c: Block(g2)
    c: Vertical(g3)
    c: Coincident(g4,g0)
    c: Horizontal(g4)
    c: Coincident(g4,g3)
    c: Coincident(g5,g1)
    c: Horizontal(g5)
    c: Block(g3)
    c: Block(g5)
FEATURE [Part::Extrusion] Extrude028  label="removeFromSolenoidDriverMainExtrude021"
  Base = -> Sketch031
  Dir = (0,0.894389,-0.447291)
  DirMode = 2
  FaceMakerClass = Part::FaceMakerBullseye
  LengthFwd = 3.1
  LengthRev = 0
  Placement = pos=(-4,-2.42,-0.8) rot=(0,0,1;0rad)
  Solid = true
  Symmetric = false
FEATURE [Part::Extrusion] Extrude029  label="solenoidDriverBottomLipTopExtrude018"
  Base = -> Sketch030
  Dir = (0,0.894389,-0.447291)
  DirMode = 2
  FaceMakerClass = Part::FaceMakerBullseye
  LengthFwd = -6.5
  LengthRev = 0
  Placement = pos=(5,-14.15,19.65) rot=(1,0,0;1.5708rad)
  Solid = true
  Symmetric = false
FEATURE [Sketcher::SketchObject] Sketch032
  FullyConstrained = true
  Placement = pos=(0,-14.3,2.37) rot=(-1,0,0;2.03453rad)
  sketch-geometry (4):
    g0: LineSegment StartX=0 StartY=1.5 StartZ=0 EndX=0 EndY=0 EndZ=0
    g1: LineSegment StartX=0 StartY=1.5 StartZ=0 EndX=5 EndY=1.5 EndZ=0
    g2: LineSegment StartX=5 StartY=1.5 StartZ=0 EndX=5 EndY=0 EndZ=0
    g3: LineSegment StartX=0 StartY=0 StartZ=0 EndX=5 EndY=0 EndZ=0
  constraints (13):
    c: Vertical(g0)
    c: Distance(g0) = 1.5
    c: Horizontal(g1)
    c: Distance(g1) = 5
    c: Coincident(g1,g0)
    c: Vertical(g2)
    c: Distance(g2) = 1.5
    c: Coincident(g2,g1)
    c: Block(g1)
    c: Block(g2)
    c: Block(g0)
    c: Coincident(g3,g0)
    c: Coincident(g3,g2)
FEATURE [Part::Extrusion] Extrude030  label="solenoidDriverBottomLipTopExtrude019"
  Base = -> Sketch032
  Dir = (0,0.894389,-0.447291)
  DirMode = 2
  FaceMakerClass = Part::FaceMakerBullseye
  LengthFwd = -6.5
  LengthRev = 0
  Placement = pos=(0,-14.15,19.65) rot=(1,0,0;1.5708rad)
  Solid = true
  Symmetric = false
FEATURE [Part::MultiFuse] Fusion004
  Placement = pos=(0,1.4,2.65) rot=(0,0,1;0rad)
  Shapes = -> [Extrude029,Extrude030]
FEATURE [Part::MultiFuse] Fusion003
  Placement = pos=(-2.3,0,0) rot=(0,0,1;0rad)
  Shapes = -> [Extrude028,Fusion004]
FEATURE [Sketcher::SketchObject] Sketch033
  FullyConstrained = true
  Placement = pos=(0,-14.3,2.37) rot=(-1,0,0;2.03453rad)
  sketch-geometry (4):
    g0: LineSegment StartX=0 StartY=1.5 StartZ=0 EndX=0 EndY=0 EndZ=0
    g1: LineSegment StartX=0 StartY=1.5 StartZ=0 EndX=5 EndY=1.5 EndZ=0
    g2: LineSegment StartX=5 StartY=1.5 StartZ=0 EndX=5 EndY=0 EndZ=0
    g3: LineSegment StartX=0 StartY=0 StartZ=0 EndX=5 EndY=0 EndZ=0
  constraints (13):
    c: Vertical(g0)
    c: Distance(g0) = 1.5
    c: Horizontal(g1)
    c: Distance(g1) = 5
    c: Coincident(g1,g0)
    c: Vertical(g2)
    c: Distance(g2) = 1.5
    c: Coincident(g2,g1)
    c: Block(g1)
    c: Block(g2)
    c: Block(g0)
    c: Coincident(g3,g0)
    c: Coincident(g3,g2)
FEATURE [Sketcher::SketchObject] Sketch034
  FullyConstrained = true
  Placement = pos=(0,-14.3,2.37) rot=(-1,0,0;2.03453rad)
  sketch-geometry (4):
    g0: LineSegment StartX=0 StartY=1.5 StartZ=0 EndX=0 EndY=0 EndZ=0
    g1: LineSegment StartX=0 StartY=1.5 StartZ=0 EndX=5 EndY=1.5 EndZ=0
    g2: LineSegment StartX=5 StartY=1.5 StartZ=0 EndX=5 EndY=0 EndZ=0
    g3: LineSegment StartX=0 StartY=0 StartZ=0 EndX=5 EndY=0 EndZ=0
  constraints (13):
    c: Vertical(g0)
    c: Distance(g0) = 1.5
    c: Horizontal(g1)
    c: Distance(g1) = 5
    c: Coincident(g1,g0)
    c: Vertical(g2)
    c: Distance(g2) = 1.5
    c: Coincident(g2,g1)
    c: Block(g1)
    c: Block(g2)
    c: Block(g0)
    c: Coincident(g3,g0)
    c: Coincident(g3,g2)
FEATURE [Part::Extrusion] Extrude020  label="removeFromSolenoidDriverMainExtrude020"
  Base = -> Sketch020
  Dir = (0,0.894389,-0.447291)
  DirMode = 2
  FaceMakerClass = Part::FaceMakerBullseye
  LengthFwd = 3.1
  LengthRev = 0
  Placement = pos=(-4,-2.42,-0.8) rot=(0,0,1;0rad)
  Solid = true
  Symmetric = false
FEATURE [Part::Fillet] Fillet
  Base = -> Fusion003
  Edges = 1 edges r=10: [Edge5]
  Placement = pos=(-2,0,0) rot=(0,0,1;0rad)
FEATURE [Part::MultiFuse] Fusion001
  Placement = pos=(0,1.4,2.65) rot=(0,0,1;0rad)
  Shapes = -> [Extrude026,Extrude027]
FEATURE [Part::MultiFuse] Fusion002
  Shapes = -> [Extrude020,Fusion001]
FEATURE [Sketcher::SketchObject] Sketch035
  FullyConstrained = true
  Placement = pos=(0,-14.3,2.37) rot=(-1,0,0;2.03453rad)
  sketch-geometry (4):
    g0: LineSegment StartX=0 StartY=1.5 StartZ=0 EndX=0 EndY=0 EndZ=0
    g1: LineSegment StartX=0 StartY=1.5 StartZ=0 EndX=5 EndY=1.5 EndZ=0
    g2: LineSegment StartX=5 StartY=1.5 StartZ=0 EndX=5 EndY=0 EndZ=0
    g3: LineSegment StartX=0 StartY=0 StartZ=0 EndX=5 EndY=0 EndZ=0
  constraints (13):
    c: Vertical(g0)
    c: Distance(g0) = 1.5
    c: Horizontal(g1)
    c: Distance(g1) = 5
    c: Coincident(g1,g0)
    c: Vertical(g2)
    c: Distance(g2) = 1.5
    c: Coincident(g2,g1)
    c: Block(g1)
    c: Block(g2)
    c: Block(g0)
    c: Coincident(g3,g0)
    c: Coincident(g3,g2)
FEATURE [Sketcher::SketchObject] Sketch036
  FullyConstrained = true
  Placement = pos=(0,-14.3,2.37) rot=(-1,0,0;2.03453rad)
  sketch-geometry (4):
    g0: LineSegment StartX=0 StartY=1.5 StartZ=0 EndX=0 EndY=0 EndZ=0
    g1: LineSegment StartX=0 StartY=1.5 StartZ=0 EndX=5 EndY=1.5 EndZ=0
    g2: LineSegment StartX=5 StartY=1.5 StartZ=0 EndX=5 EndY=0 EndZ=0
    g3: LineSegment StartX=0 StartY=0 StartZ=0 EndX=5 EndY=0 EndZ=0
  constraints (13):
    c: Vertical(g0)
    c: Distance(g0) = 1.5
    c: Horizontal(g1)
    c: Distance(g1) = 5
    c: Coincident(g1,g0)
    c: Vertical(g2)
    c: Distance(g2) = 1.5
    c: Coincident(g2,g1)
    c: Block(g1)
    c: Block(g2)
    c: Block(g0)
    c: Coincident(g3,g0)
    c: Coincident(g3,g2)
FEATURE [Part::Extrusion] Extrude031  label="solenoidDriverBottomLipTopExtrude020"
  Base = -> Sketch035
  Dir = (0,0.894389,-0.447291)
  DirMode = 2
  FaceMakerClass = Part::FaceMakerBullseye
  LengthFwd = -6.5
  LengthRev = 0
  Placement = pos=(5,-14.15,19.65) rot=(1,0,0;1.5708rad)
  Solid = true
  Symmetric = false
FEATURE [Part::Extrusion] Extrude032  label="solenoidDriverBottomLipTopExtrude021"
  Base = -> Sketch036
  Dir = (0,0.894389,-0.447291)
  DirMode = 2
  FaceMakerClass = Part::FaceMakerBullseye
  LengthFwd = -6.5
  LengthRev = 0
  Placement = pos=(0,-14.15,19.65) rot=(1,0,0;1.5708rad)
  Solid = true
  Symmetric = false
FEATURE [Part::MultiFuse] Fusion009
  Placement = pos=(8,1.4,2.65) rot=(0,0,1;0rad)
  Shapes = -> [Extrude031,Extrude032]
FEATURE [Part::MultiFuse] Fusion010  label="removeFromSolenoidDriver"
  Shapes = -> [Fusion009,Fillet,Fusion002]
FEATURE [Sketcher::SketchObject] Sketch037
  FullyConstrained = true
  Placement = pos=(0,0,0) rot=(1,0,0;1.5708rad)
  sketch-geometry (4):
    g0: Circle CenterX=64.05 CenterY=16.5 CenterZ=0 NormalX=0 NormalY=0 NormalZ=1 AngleXU=0 Radius=2.7
    g1: Circle CenterX=64.05 CenterY=8.5 CenterZ=0 NormalX=0 NormalY=0 NormalZ=1 AngleXU=0 Radius=2.7
    g2: Circle CenterX=84.15 CenterY=8.5 CenterZ=0 NormalX=0 NormalY=0 NormalZ=1 AngleXU=0 Radius=2.7
    g3: Circle CenterX=84.15 CenterY=16.5 CenterZ=0 NormalX=0 NormalY=0 NormalZ=1 AngleXU=0 Radius=2.7
  constraints (4):
    c: Block(g2)
    c: Block(g3)
    c: Block(g0)
    c: Block(g1)
FEATURE [Part::Extrusion] Extrude033  label="removeFromMainBodyToCreateScrewHoleCounterSinks001"
  Base = -> Sketch037
  Dir = (0,-1,1.1e-15)
  DirMode = 2
  FaceMakerClass = Part::FaceMakerBullseye
  LengthFwd = 1.9
  LengthRev = 0
  Placement = pos=(0.8,0,0) rot=(0,0,1;0rad)
  Solid = true
  Symmetric = false
FEATURE [Part::MultiFuse] Fusion011  label="removeFromMainBodyToCreateScrewHoleCounterSinks001Fusion011"
  Shapes = -> [Extrude014,Extrude033]
FEATURE [Sketcher::SketchObject] Sketch038
  FullyConstrained = true
  Placement = pos=(0,-14.3,2.37) rot=(-1,0,0;2.03453rad)
  sketch-geometry (4):
    g0: LineSegment StartX=33.9 StartY=-9.7 StartZ=0 EndX=33.9 EndY=-1.5 EndZ=0
    g1: LineSegment StartX=33.9 StartY=-1.5 StartZ=0 EndX=44.5 EndY=-1.5 EndZ=0
    g2: LineSegment StartX=33.9 StartY=-9.7 StartZ=0 EndX=44.5 EndY=-9.7 EndZ=0
    g3: LineSegment StartX=44.5 StartY=-1.5 StartZ=0 EndX=44.5 EndY=-9.7 EndZ=0
  constraints (10):
    c: Vertical(g0)
    c: Coincident(g1,g0)
    c: Horizontal(g1)
    c: Block(g1)
    c: Block(g0)
    c: Coincident(g2,g0)
    c: Horizontal(g2)
    c: Coincident(g3,g1)
    c: Coincident(g3,g2)
    c: Vertical(g3)
FEATURE [Part::Extrusion] Extrude034
  Base = -> Sketch038
  Dir = (0,0.894389,-0.447291)
  DirMode = 2
  FaceMakerClass = Part::FaceMakerBullseye
  LengthFwd = 16
  LengthRev = 0
  Placement = pos=(0,-22,7) rot=(0,0,1;0rad)
  Solid = true
  Symmetric = false
FEATURE [Sketcher::SketchObject] Sketch039
  FullyConstrained = true
  Placement = pos=(0,-14.3,2.37) rot=(-1,0,0;2.03453rad)
  sketch-geometry (4):
    g0: LineSegment StartX=5.5 StartY=-7.7 StartZ=0 EndX=13.3 EndY=-7.7 EndZ=0
    g1: LineSegment StartX=13.3 StartY=-7.7 StartZ=0 EndX=13.3 EndY=-13.1 EndZ=0
    g2: LineSegment StartX=13.3 StartY=-13.1 StartZ=0 EndX=5.5 EndY=-13.1 EndZ=0
    g3: LineSegment StartX=5.5 StartY=-7.7 StartZ=0 EndX=5.5 EndY=-13.1 EndZ=0
  constraints (12):
    c: Horizontal(g0)
    c: Distance(g0) = 7.8
    c: Coincident(g1,g0)
    c: Vertical(g1)
    c: Distance(g1) = 5.4
    c: Coincident(g2,g1)
    c: Horizontal(g2)
    c: Vertical(g3)
    c: Coincident(g3,g2)
    c: Block(g0)
    c: Block(g2)
    c: Block(g3)
FEATURE [Part::Extrusion] Extrude035  label="removeToMakeHoleForConnectorExtrude035"
  Base = -> Sketch039
  Dir = (0,0.894389,-0.447291)
  DirMode = 2
  FaceMakerClass = Part::FaceMakerBullseye
  LengthFwd = 15
  LengthRev = 0
  Placement = pos=(-4,-22,9.6469) rot=(0,0,1;0rad)
  Solid = true
  Symmetric = false
FEATURE [App::MeasureDistance] Distance  label="Distance: 4.00 mm"
  Distance = 4.00184
  P1 = (119.349,-15.3,8)
  P2 = (123.351,-15.3,8)
FEATURE [App::MeasureDistance] Distance001  label="Distance: 3.80 mm"
  Distance = 3.8
  P1 = (119.45,-15.3,8)
  P2 = (123.25,-15.3,8)
FEATURE [Part::Fillet] Fillet015
  Base = -> Extrude009
  Edges = 1 edges r=1.59: [Edge7]
FEATURE [Part::Fillet] Fillet016
  Base = -> Extrude017
  Edges = 1 edges r=1.49: [Edge12]
FEATURE [Part::Fillet] Fillet017
  Base = -> Fillet016
  Edges = 1 edges r=1.45: [Edge8]
FEATURE [Part::MultiFuse] Fusion012  label="main"
  Shapes = -> [Extrude,Revolve,Extrude005,Fillet003,Fillet012,Fillet014,Extrude025,Fusion,Fillet015,Fillet017]
FEATURE [Part::Cut] Cut001
  Base = -> Fusion012
  Tool = -> Box003
FEATURE [Part::Cut] Cut002
  Base = -> Cut001
  Tool = -> Box002
FEATURE [Part::Cut] Cut003
  Base = -> Cut002
  Tool = -> Cut
FEATURE [Part::Cut] Cut004
  Base = -> Cut003
  Tool = -> Extrude019
FEATURE [Part::Cut] Cut005
  Base = -> Cut004
  Tool = -> Fusion011
FEATURE [Part::Cut] Cut006
  Base = -> Cut005
  Tool = -> Extrude004
FEATURE [Part::Cut] Cut007
  Base = -> Cut006
  Tool = -> Extrude015
FEATURE [Part::Cut] Cut008
  Base = -> Cut007
  Tool = -> Extrude008
FEATURE [Part::Cut] Cut009
  Base = -> Cut008
  Tool = -> Fusion010
FEATURE [App::MeasureDistance] Distance002  label="Distance: 2.05 mm"
  Distance = 2.05453
  P1 = (1.5,-23.0732,21.402)
  P2 = (6e-15,-23,20)
FEATURE [Part::Cut] Cut010
  Base = -> Cut009
  Tool = -> Extrude035
FEATURE [Part::Cut] Cut011
  Base = -> Cut010
  Tool = -> Extrude034
FEATURE [Part::Box] Box004  label="Cube004"
  AttacherType = Attacher::AttachEngine3D
  Height = 10
  Length = 200
  Placement = pos=(-30,0,0) rot=(0,0,1;0rad)
  Width = 10
FEATURE [Part::Fillet] Fillet020
  Base = -> Box004
  Edges = 1 edges r=3.6: [Edge12]
FEATURE [Part::Box] Box005  label="Cube005"
  AttacherType = Attacher::AttachEngine3D
  Height = 10
  Length = 198
  Placement = pos=(-30,0,0) rot=(0,0,1;0rad)
  Width = 10
FEATURE [Part::Cut] Cut012
  Base = -> Box005
  Tool = -> Fillet020
FEATURE [Part::Box] Box006  label="Cube006"
  AttacherType = Attacher::AttachEngine3D
  Height = 5
  Length = 200
  Placement = pos=(-30,6.4,10) rot=(1,0,0;0rad)
  Width = 5
FEATURE [Part::Box] Box007  label="Cube007"
  AttacherType = Attacher::AttachEngine3D
  Height = 5
  Length = 200
  Placement = pos=(-30,6.4,10) rot=(1,0,0;0.872665rad)
  Width = 5
FEATURE [Part::MultiFuse] Fusion013  label="removeFromMainFusion013"
  Placement = pos=(0,-10,10) rot=(0,0,1;0rad)
  Shapes = -> [Box007,Box006,Cut012]
FEATURE [Mesh::Feature] v0_98_Cut013  label="v0_98-Cut013"
FEATURE [App::MeasureDistance] Distance003  label="Distance: 7.18 mm"
  Distance = 7.17719
  P1 = (117.773,-15.3145,-2.4)
  P2 = (124.951,-15.2973,-2.4)
FEATURE [Sketcher::SketchObject] Sketch040
  FullyConstrained = true
  Placement = pos=(0,-14.3,2.37) rot=(-1,0,0;2.03453rad)
  sketch-geometry (4):
    g0: LineSegment StartX=0 StartY=1.5 StartZ=0 EndX=0 EndY=0 EndZ=0
    g1: LineSegment StartX=0 StartY=1.5 StartZ=0 EndX=5 EndY=1.5 EndZ=0
    g2: LineSegment StartX=5 StartY=1.5 StartZ=0 EndX=5 EndY=0 EndZ=0
    g3: LineSegment StartX=0 StartY=0 StartZ=0 EndX=5 EndY=0 EndZ=0
  constraints (13):
    c: Vertical(g0)
    c: Distance(g0) = 1.5
    c: Horizontal(g1)
    c: Distance(g1) = 5
    c: Coincident(g1,g0)
    c: Vertical(g2)
    c: Distance(g2) = 1.5
    c: Coincident(g2,g1)
    c: Block(g1)
    c: Block(g2)
    c: Block(g0)
    c: Coincident(g3,g0)
    c: Coincident(g3,g2)
FEATURE [Part::Extrusion] Extrude036
  Base = -> Sketch040
  Dir = (0,0.894389,-0.447291)
  DirMode = 2
  FaceMakerClass = Part::FaceMakerBullseye
  LengthFwd = 1.4
  LengthRev = 0
  Placement = pos=(0,8.25,17.58) rot=(0,0,1;0rad)
  Solid = true
  Symmetric = false
FEATURE [Sketcher::SketchObject] Sketch041
  FullyConstrained = true
  Placement = pos=(0,-14.3,2.37) rot=(-1,0,0;2.03453rad)
  sketch-geometry (4):
    g0: LineSegment StartX=0 StartY=1.5 StartZ=0 EndX=0 EndY=0 EndZ=0
    g1: LineSegment StartX=0 StartY=1.5 StartZ=0 EndX=5 EndY=1.5 EndZ=0
    g2: LineSegment StartX=5 StartY=1.5 StartZ=0 EndX=5 EndY=0 EndZ=0
    g3: LineSegment StartX=0 StartY=0 StartZ=0 EndX=5 EndY=0 EndZ=0
  constraints (13):
    c: Vertical(g0)
    c: Distance(g0) = 1.5
    c: Horizontal(g1)
    c: Distance(g1) = 5
    c: Coincident(g1,g0)
    c: Vertical(g2)
    c: Distance(g2) = 1.5
    c: Coincident(g2,g1)
    c: Block(g1)
    c: Block(g2)
    c: Block(g0)
    c: Coincident(g3,g0)
    c: Coincident(g3,g2)
FEATURE [Part::Extrusion] Extrude037
  Base = -> Sketch041
  Dir = (0,0.894389,-0.447291)
  DirMode = 2
  FaceMakerClass = Part::FaceMakerBullseye
  LengthFwd = 1.4
  LengthRev = 0
  Placement = pos=(0,6.11,13.33) rot=(0,0,1;0rad)
  Solid = true
  Symmetric = false
FEATURE [Part::MultiFuse] Fusion014  label="screwSpacerFusion014"
  Shapes = -> [Extrude037,Extrude036]
FEATURE [Sketcher::SketchObject] Sketch042
  FullyConstrained = true
  Placement = pos=(0,-14.3,2.37) rot=(-1,0,0;2.03453rad)
  sketch-geometry (4):
    g0: LineSegment StartX=0 StartY=1.5 StartZ=0 EndX=0 EndY=0 EndZ=0
    g1: LineSegment StartX=0 StartY=1.5 StartZ=0 EndX=5 EndY=1.5 EndZ=0
    g2: LineSegment StartX=5 StartY=1.5 StartZ=0 EndX=5 EndY=0 EndZ=0
    g3: LineSegment StartX=0 StartY=0 StartZ=0 EndX=5 EndY=0 EndZ=0
  constraints (13):
    c: Vertical(g0)
    c: Distance(g0) = 1.5
    c: Horizontal(g1)
    c: Distance(g1) = 5
    c: Coincident(g1,g0)
    c: Vertical(g2)
    c: Distance(g2) = 1.5
    c: Coincident(g2,g1)
    c: Block(g1)
    c: Block(g2)
    c: Block(g0)
    c: Coincident(g3,g0)
    c: Coincident(g3,g2)
FEATURE [Part::Extrusion] Extrude038
  Base = -> Sketch042
  Dir = (0,0.894389,-0.447291)
  DirMode = 2
  FaceMakerClass = Part::FaceMakerBullseye
  LengthFwd = 1.4
  LengthRev = 0
  Placement = pos=(0,8.459,18) rot=(0,0,1;0rad)
  Solid = true
  Symmetric = false
FEATURE [Part::MultiFuse] Fusion015  label="screwSpacerFusion014Fusion015"
  Placement = pos=(0,0.35,-0.18) rot=(0,0,1;0rad)
  Shapes = -> [Extrude038,Fusion014]
FEATURE [Part::Cylinder] Cylinder
  Angle = 360
  AttacherType = Attacher::AttachEngine3D
  Height = 10
  Placement = pos=(0,10,0) rot=(0,0,1;0rad)
  Radius = 1.5
FEATURE [Part::Cylinder] Cylinder001
  Angle = 360
  AttacherType = Attacher::AttachEngine3D
  Height = 10
  Placement = pos=(3,10,0) rot=(0,0,1;0rad)
  Radius = 1.5
FEATURE [Part::Box] Box008  label="Cube008"
  AttacherType = Attacher::AttachEngine3D
  Height = 10
  Length = 3
  Placement = pos=(0,8.5,0) rot=(0,0,1;0rad)
  Width = 3
FEATURE [Part::MultiFuse] Fusion016  label="holeForWireFusion016"
  Shapes = -> [Cylinder001,Box008,Cylinder]
FEATURE [Part::Box] Box009  label="Cube009"
  AttacherType = Attacher::AttachEngine3D
  Height = 10
  Length = 3
  Placement = pos=(0,8.5,0) rot=(0,0,1;0rad)
  Width = 3
FEATURE [Part::Cylinder] Cylinder002
  Angle = 360
  AttacherType = Attacher::AttachEngine3D
  Height = 10
  Placement = pos=(0,10,0) rot=(0,0,1;0rad)
  Radius = 1.5
FEATURE [Part::Cylinder] Cylinder003
  Angle = 360
  AttacherType = Attacher::AttachEngine3D
  Height = 10
  Placement = pos=(3,10,0) rot=(0,0,1;0rad)
  Radius = 1.5
FEATURE [Part::MultiFuse] Fusion017  label="holeForWireFusion017"
  Placement = pos=(0,0,10) rot=(0,0,1;0rad)
  Shapes = -> [Cylinder003,Box009,Cylinder002]
FEATURE [Part::MultiFuse] Fusion018  label="holeForWireFusion018"
  Placement = pos=(0,0,0) rot=(0,1,0;-1.5708rad)
  Shapes = -> [Fusion017,Fusion016]
FEATURE [Part::Box] Box010  label="Cube010"
  AttacherType = Attacher::AttachEngine3D
  Height = 0.1
  Length = 0.1
  Placement = pos=(-2,10,0) rot=(0,0.995037,0.099504;0rad)
  Width = 0.1
FEATURE [Part::MultiFuse] Fusion019
  Placement = pos=(0,10,0) rot=(1,0,0;1.5708rad)
  Shapes = -> [Box010,Fusion018]
FEATURE [Part::Box] Box011  label="Cube011"
  AttacherType = Attacher::AttachEngine3D
  Height = 0.1
  Length = 1.1
  Placement = pos=(-2,10,10) rot=(0,0.995037,0.099504;0rad)
  Width = 0.1
FEATURE [Part::MultiFuse] Fusion020
  Placement = pos=(0,0,0) rot=(0,1,0;0.349066rad)
  Shapes = -> [Box011,Fusion019]
FEATURE [Part::Box] Box012  label="Cube012"
  AttacherType = Attacher::AttachEngine3D
  Height = 0.1
  Length = 1.1
  Placement = pos=(-2,10,10) rot=(0,0.995037,0.099504;0rad)
  Width = 0.1
FEATURE [Part::MultiFuse] Fusion021
  Placement = pos=(0,30,0) rot=(0,0,1;-2.6529rad)
  Shapes = -> [Box012,Fusion020]
FEATURE [Part::Box] Box013  label="Cube013"
  AttacherType = Attacher::AttachEngine3D
  Height = 0.1
  Length = 1.1
  Placement = pos=(2,19,10) rot=(0,0.995037,0.099504;0rad)
  Width = 0.1
FEATURE [Part::MultiFuse] Fusion022  label="holeForWire"
  Placement = pos=(15,-49.8,-8.2) rot=(0,0,1;0rad)
  Shapes = -> [Box013,Fusion021]
FEATURE [Part::Cut] Cut013
  Base = -> Cut011
  Tool = -> Fusion013
FEATURE [Part::Cut] Cut014
  Base = -> Cut013
  Tool = -> Fusion022
FEATURE [Sketcher::SketchObject] Sketch043
  FullyConstrained = true
  MapMode = 4
  Placement = pos=(0,0,0) rot=(0.57735,0.57735,0.57735;2.0944rad)
  Support = -> [Cut014]
  sketch-geometry (14):
    g0: LineSegment StartX=6.08745 StartY=-4.11588 StartZ=0 EndX=6.08745 EndY=-2.11589 EndZ=0
    g1: LineSegment StartX=3.58745 StartY=2.38411 StartZ=0 EndX=3.58745 EndY=4.38411 EndZ=0
    g2: LineSegment StartX=8.08745 StartY=1.38411 StartZ=0 EndX=8.08745 EndY=-1.11589 EndZ=0
    g3: ArcOfCircle CenterX=7.08745 CenterY=-1.11589 CenterZ=0 NormalX=0 NormalY=0 NormalZ=1 AngleXU=0 Radius=1 StartAngle=4.71239 EndAngle=6.28319
    g4: LineSegment StartX=6.08745 StartY=-2.11589 StartZ=0 EndX=7.08745 EndY=-2.11589 EndZ=0
    g5: LineSegment StartX=6.08745 StartY=-4.11588 StartZ=0 EndX=7.08745 EndY=-4.11588 EndZ=0
    g6: ArcOfCircle CenterX=7.08745 CenterY=-1.11589 CenterZ=0 NormalX=0 NormalY=0 NormalZ=1 AngleXU=0 Radius=3 StartAngle=4.71239 EndAngle=6.28319
    g7: ArcOfCircle CenterX=7.08745 CenterY=1.38411 CenterZ=0 NormalX=0 NormalY=0 NormalZ=1 AngleXU=0 Radius=1 StartAngle=5.35e-14 EndAngle=1.5708
    g8: LineSegment StartX=3.58745 StartY=4.38411 StartZ=0 EndX=7.08745 EndY=4.38411 EndZ=0
    g9: LineSegment StartX=10.0875 StartY=-1.11588 StartZ=0 EndX=10.0875 EndY=1.38411 EndZ=0
    g10: ArcOfCircle CenterX=7.08745 CenterY=1.38411 CenterZ=0 NormalX=0 NormalY=0 NormalZ=1 AngleXU=0 Radius=3 StartAngle=3.57e-14 EndAngle=1.5708
    g11: LineSegment StartX=3.58745 StartY=2.38411 StartZ=0 EndX=3.58745 EndY=1.38411 EndZ=0
    g12: ArcOfCircle CenterX=4.58745 CenterY=1.38412 CenterZ=0 NormalX=0 NormalY=0 NormalZ=1 AngleXU=0 Radius=1 StartAngle=1.57081 EndAngle=3.14159
    g13: LineSegment StartX=4.58744 StartY=2.38411 StartZ=0 EndX=7.08745 EndY=2.38411 EndZ=0
  constraints (33):
    c: Vertical(g0)
    c: Vertical(g1)
    c: Distance(g1) = 2
    c: Block(g0)
    c: Block(g2)
    c: Coincident(g3,g2)
    c: Coincident(g4,g0)
    c: Coincident(g4,g3)
    c: Horizontal(g4)
    c: Block(g3)
    c: Coincident(g5,g0)
    c: Horizontal(g5)
    c: Coincident(g6,g3)
    c: Block(g6)
    c: Block(g5)
    c: Coincident(g7,g2)
    c: Block(g7)
    c: Coincident(g8,g1)
    c: Coincident(g9,g6)
    c: Vertical(g9)
    c: Coincident(g10,g7)
    c: Block(g10)
    c: Block(g8)
    c: Block(g9)
    c: Coincident(g11,g1)
    c: Vertical(g11)
    c: Distance(g11) = 1
    c: Coincident(g12,g11)
    c: Coincident(g13,g12)
    c: Coincident(g13,g7)
    c: Horizontal(g13)
    c: Block(g13)
    c: Block(g12)
FEATURE [Sketcher::SketchObject] Sketch044
  FullyConstrained = true
  MapMode = 4
  Placement = pos=(0,0,0) rot=(0.57735,0.57735,0.57735;2.0944rad)
  Support = -> [Cut014]
  sketch-geometry (14):
    g0: LineSegment StartX=6.08745 StartY=-4.11588 StartZ=0 EndX=6.08745 EndY=-2.11589 EndZ=0
    g1: LineSegment StartX=8.08745 StartY=1.38411 StartZ=0 EndX=8.08745 EndY=-1.11589 EndZ=0
    g2: ArcOfCircle CenterX=7.08745 CenterY=-1.11589 CenterZ=0 NormalX=0 NormalY=0 NormalZ=1 AngleXU=0 Radius=1 StartAngle=4.71239 EndAngle=6.28319
    g3: LineSegment StartX=6.08745 StartY=-2.11589 StartZ=0 EndX=7.08745 EndY=-2.11589 EndZ=0
    g4: LineSegment StartX=6.08745 StartY=-4.11588 StartZ=0 EndX=7.08745 EndY=-4.11588 EndZ=0
    g5: ArcOfCircle CenterX=7.08745 CenterY=-1.11589 CenterZ=0 NormalX=0 NormalY=0 NormalZ=1 AngleXU=0 Radius=3 StartAngle=4.71239 EndAngle=6.28319
    g6: ArcOfCircle CenterX=7.08745 CenterY=1.38411 CenterZ=0 NormalX=0 NormalY=0 NormalZ=1 AngleXU=0 Radius=1 StartAngle=5.35e-14 EndAngle=1.5708
    g7: LineSegment StartX=10.0875 StartY=-1.11588 StartZ=0 EndX=10.0875 EndY=1.38411 EndZ=0
    g8: ArcOfCircle CenterX=7.08745 CenterY=1.38411 CenterZ=0 NormalX=0 NormalY=0 NormalZ=1 AngleXU=0 Radius=3 StartAngle=3.57e-14 EndAngle=1.5708
    g9: ArcOfCircle CenterX=4.58745 CenterY=1.38412 CenterZ=0 NormalX=0 NormalY=0 NormalZ=1 AngleXU=0 Radius=1 StartAngle=1.57081 EndAngle=3.14159
    g10: LineSegment StartX=4.58744 StartY=2.38411 StartZ=0 EndX=7.08745 EndY=2.38411 EndZ=0
    g11: LineSegment StartX=4.58745 StartY=4.38411 StartZ=0 EndX=7.08745 EndY=4.38411 EndZ=0
    g12: ArcOfCircle CenterX=4.58745 CenterY=5.38411 CenterZ=0 NormalX=0 NormalY=0 NormalZ=1 AngleXU=0 Radius=1 StartAngle=3.14159 EndAngle=4.71239
    g13: LineSegment StartX=3.58745 StartY=5.38411 StartZ=0 EndX=3.58745 EndY=1.38411 EndZ=0
  constraints (33):
    c: Vertical(g0)
    c: Block(g0)
    c: Block(g1)
    c: Coincident(g2,g1)
    c: Coincident(g3,g0)
    c: Coincident(g3,g2)
    c: Horizontal(g3)
    c: Block(g2)
    c: Coincident(g4,g0)
    c: Horizontal(g4)
    c: Coincident(g5,g2)
    c: Block(g5)
    c: Block(g4)
    c: Coincident(g6,g1)
    c: Block(g6)
    c: Coincident(g7,g5)
    c: Vertical(g7)
    c: Coincident(g8,g6)
    c: Block(g8)
    c: Block(g7)
    c: Coincident(g10,g9)
    c: Coincident(g10,g6)
    c: Horizontal(g10)
    c: Block(g10)
    c: Block(g9)
    c: Coincident(g11,g8)
    c: Horizontal(g11)
    c: Block(g12)
    c: Block(g11)
    c: Coincident(g13,g12)
    c: Coincident(g13,g9)
    c: Vertical(g13)
    c: Tangent(g13,g9)
FEATURE [Part::Extrusion] Extrude039
  Base = -> Sketch044
  Dir = (1,0,0)
  DirMode = 2
  FaceMakerClass = Part::FaceMakerBullseye
  LengthFwd = 10
  LengthRev = 0
  Placement = pos=(8,-22.615,4.115) rot=(0,0,1;3.14159rad)
  Solid = true
  Symmetric = false
FEATURE [App::MeasureDistance] Distance004  label="Distance: 42.16 mm"
  Distance = 42.1607
  P1 = (14.6786,-26.2,1.24491)
  P2 = (-27.4815,-26.2,1.03853)
FEATURE [Sketcher::SketchObject] Sketch045
  FullyConstrained = true
  MapMode = 4
  Placement = pos=(0,0,0) rot=(0.57735,0.57735,0.57735;2.0944rad)
  Support = -> [Cut014]
  sketch-geometry (14):
    g0: LineSegment StartX=6.08745 StartY=-4.11588 StartZ=0 EndX=6.08745 EndY=-2.11589 EndZ=0
    g1: LineSegment StartX=8.08745 StartY=1.38411 StartZ=0 EndX=8.08745 EndY=-1.11589 EndZ=0
    g2: ArcOfCircle CenterX=7.08745 CenterY=-1.11589 CenterZ=0 NormalX=0 NormalY=0 NormalZ=1 AngleXU=0 Radius=1 StartAngle=4.71239 EndAngle=6.28319
    g3: LineSegment StartX=6.08745 StartY=-2.11589 StartZ=0 EndX=7.08745 EndY=-2.11589 EndZ=0
    g4: LineSegment StartX=6.08745 StartY=-4.11588 StartZ=0 EndX=7.08745 EndY=-4.11588 EndZ=0
    g5: ArcOfCircle CenterX=7.08745 CenterY=-1.11589 CenterZ=0 NormalX=0 NormalY=0 NormalZ=1 AngleXU=0 Radius=3 StartAngle=4.71239 EndAngle=6.28319
    g6: ArcOfCircle CenterX=7.08745 CenterY=1.38411 CenterZ=0 NormalX=0 NormalY=0 NormalZ=1 AngleXU=0 Radius=1 StartAngle=5.35e-14 EndAngle=1.5708
    g7: LineSegment StartX=10.0875 StartY=-1.11588 StartZ=0 EndX=10.0875 EndY=1.38411 EndZ=0
    g8: ArcOfCircle CenterX=7.08745 CenterY=1.38411 CenterZ=0 NormalX=0 NormalY=0 NormalZ=1 AngleXU=0 Radius=3 StartAngle=3.57e-14 EndAngle=1.5708
    g9: ArcOfCircle CenterX=4.58745 CenterY=1.38412 CenterZ=0 NormalX=0 NormalY=0 NormalZ=1 AngleXU=0 Radius=1 StartAngle=1.57081 EndAngle=3.14159
    g10: LineSegment StartX=4.58744 StartY=2.38411 StartZ=0 EndX=7.08745 EndY=2.38411 EndZ=0
    g11: LineSegment StartX=4.58745 StartY=4.38411 StartZ=0 EndX=7.08745 EndY=4.38411 EndZ=0
    g12: ArcOfCircle CenterX=4.58745 CenterY=5.38411 CenterZ=0 NormalX=0 NormalY=0 NormalZ=1 AngleXU=0 Radius=1 StartAngle=3.14159 EndAngle=4.71239
    g13: LineSegment StartX=3.58745 StartY=5.38411 StartZ=0 EndX=3.58745 EndY=1.38411 EndZ=0
  constraints (33):
    c: Vertical(g0)
    c: Block(g0)
    c: Block(g1)
    c: Coincident(g2,g1)
    c: Coincident(g3,g0)
    c: Coincident(g3,g2)
    c: Horizontal(g3)
    c: Block(g2)
    c: Coincident(g4,g0)
    c: Horizontal(g4)
    c: Coincident(g5,g2)
    c: Block(g5)
    c: Block(g4)
    c: Coincident(g6,g1)
    c: Block(g6)
    c: Coincident(g7,g5)
    c: Vertical(g7)
    c: Coincident(g8,g6)
    c: Block(g8)
    c: Block(g7)
    c: Coincident(g10,g9)
    c: Coincident(g10,g6)
    c: Horizontal(g10)
    c: Block(g10)
    c: Block(g9)
    c: Coincident(g11,g8)
    c: Horizontal(g11)
    c: Block(g12)
    c: Block(g11)
    c: Coincident(g13,g12)
    c: Coincident(g13,g9)
    c: Vertical(g13)
    c: Tangent(g13,g9)
FEATURE [Part::Extrusion] Extrude040
  Base = -> Sketch045
  Dir = (1,0,0)
  DirMode = 2
  FaceMakerClass = Part::FaceMakerBullseye
  LengthFwd = 10
  LengthRev = 0
  Placement = pos=(-17.5,-22.615,4.115) rot=(0,0,1;3.14159rad)
  Solid = true
  Symmetric = false
FEATURE [Sketcher::SketchObject] Sketch046
  FullyConstrained = true
  MapMode = 4
  Placement = pos=(0,0,0) rot=(0.57735,0.57735,0.57735;2.0944rad)
  Support = -> [Cut014]
  sketch-geometry (14):
    g0: LineSegment StartX=6.08745 StartY=-4.11588 StartZ=0 EndX=6.08745 EndY=-2.11589 EndZ=0
    g1: LineSegment StartX=8.08745 StartY=1.38411 StartZ=0 EndX=8.08745 EndY=-1.11589 EndZ=0
    g2: ArcOfCircle CenterX=7.08745 CenterY=-1.11589 CenterZ=0 NormalX=0 NormalY=0 NormalZ=1 AngleXU=0 Radius=1 StartAngle=4.71239 EndAngle=6.28319
    g3: LineSegment StartX=6.08745 StartY=-2.11589 StartZ=0 EndX=7.08745 EndY=-2.11589 EndZ=0
    g4: LineSegment StartX=6.08745 StartY=-4.11588 StartZ=0 EndX=7.08745 EndY=-4.11588 EndZ=0
    g5: ArcOfCircle CenterX=7.08745 CenterY=-1.11589 CenterZ=0 NormalX=0 NormalY=0 NormalZ=1 AngleXU=0 Radius=3 StartAngle=4.71239 EndAngle=6.28319
    g6: ArcOfCircle CenterX=7.08745 CenterY=1.38411 CenterZ=0 NormalX=0 NormalY=0 NormalZ=1 AngleXU=0 Radius=1 StartAngle=5.35e-14 EndAngle=1.5708
    g7: LineSegment StartX=10.0875 StartY=-1.11588 StartZ=0 EndX=10.0875 EndY=1.38411 EndZ=0
    g8: ArcOfCircle CenterX=7.08745 CenterY=1.38411 CenterZ=0 NormalX=0 NormalY=0 NormalZ=1 AngleXU=0 Radius=3 StartAngle=3.57e-14 EndAngle=1.5708
    g9: ArcOfCircle CenterX=4.58745 CenterY=1.38412 CenterZ=0 NormalX=0 NormalY=0 NormalZ=1 AngleXU=0 Radius=1 StartAngle=1.57081 EndAngle=3.14159
    g10: LineSegment StartX=4.58744 StartY=2.38411 StartZ=0 EndX=7.08745 EndY=2.38411 EndZ=0
    g11: LineSegment StartX=4.58745 StartY=4.38411 StartZ=0 EndX=7.08745 EndY=4.38411 EndZ=0
    g12: ArcOfCircle CenterX=4.58745 CenterY=5.38411 CenterZ=0 NormalX=0 NormalY=0 NormalZ=1 AngleXU=0 Radius=1 StartAngle=3.14159 EndAngle=4.71239
    g13: LineSegment StartX=3.58745 StartY=5.38411 StartZ=0 EndX=3.58745 EndY=1.38411 EndZ=0
  constraints (33):
    c: Vertical(g0)
    c: Block(g0)
    c: Block(g1)
    c: Coincident(g2,g1)
    c: Coincident(g3,g0)
    c: Coincident(g3,g2)
    c: Horizontal(g3)
    c: Block(g2)
    c: Coincident(g4,g0)
    c: Horizontal(g4)
    c: Coincident(g5,g2)
    c: Block(g5)
    c: Block(g4)
    c: Coincident(g6,g1)
    c: Block(g6)
    c: Coincident(g7,g5)
    c: Vertical(g7)
    c: Coincident(g8,g6)
    c: Block(g8)
    c: Block(g7)
    c: Coincident(g10,g9)
    c: Coincident(g10,g6)
    c: Horizontal(g10)
    c: Block(g10)
    c: Block(g9)
    c: Coincident(g11,g8)
    c: Horizontal(g11)
    c: Block(g12)
    c: Block(g11)
    c: Coincident(g13,g12)
    c: Coincident(g13,g9)
    c: Vertical(g13)
    c: Tangent(g13,g9)
FEATURE [Sketcher::SketchObject] Sketch047
  FullyConstrained = true
  MapMode = 4
  Placement = pos=(0,0,0) rot=(0.57735,0.57735,0.57735;2.0944rad)
  Support = -> [Cut014]
  sketch-geometry (14):
    g0: LineSegment StartX=6.08745 StartY=-4.11588 StartZ=0 EndX=6.08745 EndY=-2.11589 EndZ=0
    g1: LineSegment StartX=8.08745 StartY=1.38411 StartZ=0 EndX=8.08745 EndY=-1.11589 EndZ=0
    g2: ArcOfCircle CenterX=7.08745 CenterY=-1.11589 CenterZ=0 NormalX=0 NormalY=0 NormalZ=1 AngleXU=0 Radius=1 StartAngle=4.71239 EndAngle=6.28319
    g3: LineSegment StartX=6.08745 StartY=-2.11589 StartZ=0 EndX=7.08745 EndY=-2.11589 EndZ=0
    g4: LineSegment StartX=6.08745 StartY=-4.11588 StartZ=0 EndX=7.08745 EndY=-4.11588 EndZ=0
    g5: ArcOfCircle CenterX=7.08745 CenterY=-1.11589 CenterZ=0 NormalX=0 NormalY=0 NormalZ=1 AngleXU=0 Radius=3 StartAngle=4.71239 EndAngle=6.28319
    g6: ArcOfCircle CenterX=7.08745 CenterY=1.38411 CenterZ=0 NormalX=0 NormalY=0 NormalZ=1 AngleXU=0 Radius=1 StartAngle=5.35e-14 EndAngle=1.5708
    g7: LineSegment StartX=10.0875 StartY=-1.11588 StartZ=0 EndX=10.0875 EndY=1.38411 EndZ=0
    g8: ArcOfCircle CenterX=7.08745 CenterY=1.38411 CenterZ=0 NormalX=0 NormalY=0 NormalZ=1 AngleXU=0 Radius=3 StartAngle=3.57e-14 EndAngle=1.5708
    g9: ArcOfCircle CenterX=4.58745 CenterY=1.38412 CenterZ=0 NormalX=0 NormalY=0 NormalZ=1 AngleXU=0 Radius=1 StartAngle=1.57081 EndAngle=3.14159
    g10: LineSegment StartX=4.58744 StartY=2.38411 StartZ=0 EndX=7.08745 EndY=2.38411 EndZ=0
    g11: LineSegment StartX=4.58745 StartY=4.38411 StartZ=0 EndX=7.08745 EndY=4.38411 EndZ=0
    g12: ArcOfCircle CenterX=4.58745 CenterY=5.38411 CenterZ=0 NormalX=0 NormalY=0 NormalZ=1 AngleXU=0 Radius=1 StartAngle=3.14159 EndAngle=4.71239
    g13: LineSegment StartX=3.58745 StartY=5.38411 StartZ=0 EndX=3.58745 EndY=1.38411 EndZ=0
  constraints (33):
    c: Vertical(g0)
    c: Block(g0)
    c: Block(g1)
    c: Coincident(g2,g1)
    c: Coincident(g3,g0)
    c: Coincident(g3,g2)
    c: Horizontal(g3)
    c: Block(g2)
    c: Coincident(g4,g0)
    c: Horizontal(g4)
    c: Coincident(g5,g2)
    c: Block(g5)
    c: Block(g4)
    c: Coincident(g6,g1)
    c: Block(g6)
    c: Coincident(g7,g5)
    c: Vertical(g7)
    c: Coincident(g8,g6)
    c: Block(g8)
    c: Block(g7)
    c: Coincident(g10,g9)
    c: Coincident(g10,g6)
    c: Horizontal(g10)
    c: Block(g10)
    c: Block(g9)
    c: Coincident(g11,g8)
    c: Horizontal(g11)
    c: Block(g12)
    c: Block(g11)
    c: Coincident(g13,g12)
    c: Coincident(g13,g9)
    c: Vertical(g13)
    c: Tangent(g13,g9)
FEATURE [Sketcher::SketchObject] Sketch048
  FullyConstrained = true
  MapMode = 4
  Placement = pos=(0,0,0) rot=(0.57735,0.57735,0.57735;2.0944rad)
  Support = -> [Cut014]
  sketch-geometry (14):
    g0: LineSegment StartX=6.08745 StartY=-4.11588 StartZ=0 EndX=6.08745 EndY=-2.11589 EndZ=0
    g1: LineSegment StartX=8.08745 StartY=1.38411 StartZ=0 EndX=8.08745 EndY=-1.11589 EndZ=0
    g2: ArcOfCircle CenterX=7.08745 CenterY=-1.11589 CenterZ=0 NormalX=0 NormalY=0 NormalZ=1 AngleXU=0 Radius=1 StartAngle=4.71239 EndAngle=6.28319
    g3: LineSegment StartX=6.08745 StartY=-2.11589 StartZ=0 EndX=7.08745 EndY=-2.11589 EndZ=0
    g4: LineSegment StartX=6.08745 StartY=-4.11588 StartZ=0 EndX=7.08745 EndY=-4.11588 EndZ=0
    g5: ArcOfCircle CenterX=7.08745 CenterY=-1.11589 CenterZ=0 NormalX=0 NormalY=0 NormalZ=1 AngleXU=0 Radius=3 StartAngle=4.71239 EndAngle=6.28319
    g6: ArcOfCircle CenterX=7.08745 CenterY=1.38411 CenterZ=0 NormalX=0 NormalY=0 NormalZ=1 AngleXU=0 Radius=1 StartAngle=5.35e-14 EndAngle=1.5708
    g7: LineSegment StartX=10.0875 StartY=-1.11588 StartZ=0 EndX=10.0875 EndY=1.38411 EndZ=0
    g8: ArcOfCircle CenterX=7.08745 CenterY=1.38411 CenterZ=0 NormalX=0 NormalY=0 NormalZ=1 AngleXU=0 Radius=3 StartAngle=3.57e-14 EndAngle=1.5708
    g9: ArcOfCircle CenterX=4.58745 CenterY=1.38412 CenterZ=0 NormalX=0 NormalY=0 NormalZ=1 AngleXU=0 Radius=1 StartAngle=1.57081 EndAngle=3.14159
    g10: LineSegment StartX=4.58744 StartY=2.38411 StartZ=0 EndX=7.08745 EndY=2.38411 EndZ=0
    g11: LineSegment StartX=4.58745 StartY=4.38411 StartZ=0 EndX=7.08745 EndY=4.38411 EndZ=0
    g12: ArcOfCircle CenterX=4.58745 CenterY=5.38411 CenterZ=0 NormalX=0 NormalY=0 NormalZ=1 AngleXU=0 Radius=1 StartAngle=3.14159 EndAngle=4.71239
    g13: LineSegment StartX=3.58745 StartY=5.38411 StartZ=0 EndX=3.58745 EndY=1.38411 EndZ=0
  constraints (33):
    c: Vertical(g0)
    c: Block(g0)
    c: Block(g1)
    c: Coincident(g2,g1)
    c: Coincident(g3,g0)
    c: Coincident(g3,g2)
    c: Horizontal(g3)
    c: Block(g2)
    c: Coincident(g4,g0)
    c: Horizontal(g4)
    c: Coincident(g5,g2)
    c: Block(g5)
    c: Block(g4)
    c: Coincident(g6,g1)
    c: Block(g6)
    c: Coincident(g7,g5)
    c: Vertical(g7)
    c: Coincident(g8,g6)
    c: Block(g8)
    c: Block(g7)
    c: Coincident(g10,g9)
    c: Coincident(g10,g6)
    c: Horizontal(g10)
    c: Block(g10)
    c: Block(g9)
    c: Coincident(g11,g8)
    c: Horizontal(g11)
    c: Block(g12)
    c: Block(g11)
    c: Coincident(g13,g12)
    c: Coincident(g13,g9)
    c: Vertical(g13)
    c: Tangent(g13,g9)
FEATURE [Sketcher::SketchObject] Sketch049
  FullyConstrained = true
  MapMode = 4
  Placement = pos=(0,0,0) rot=(0.57735,0.57735,0.57735;2.0944rad)
  Support = -> [Cut014]
  sketch-geometry (14):
    g0: LineSegment StartX=6.08745 StartY=-4.11588 StartZ=0 EndX=6.08745 EndY=-2.11589 EndZ=0
    g1: LineSegment StartX=8.08745 StartY=1.38411 StartZ=0 EndX=8.08745 EndY=-1.11589 EndZ=0
    g2: ArcOfCircle CenterX=7.08745 CenterY=-1.11589 CenterZ=0 NormalX=0 NormalY=0 NormalZ=1 AngleXU=0 Radius=1 StartAngle=4.71239 EndAngle=6.28319
    g3: LineSegment StartX=6.08745 StartY=-2.11589 StartZ=0 EndX=7.08745 EndY=-2.11589 EndZ=0
    g4: LineSegment StartX=6.08745 StartY=-4.11588 StartZ=0 EndX=7.08745 EndY=-4.11588 EndZ=0
    g5: ArcOfCircle CenterX=7.08745 CenterY=-1.11589 CenterZ=0 NormalX=0 NormalY=0 NormalZ=1 AngleXU=0 Radius=3 StartAngle=4.71239 EndAngle=6.28319
    g6: ArcOfCircle CenterX=7.08745 CenterY=1.38411 CenterZ=0 NormalX=0 NormalY=0 NormalZ=1 AngleXU=0 Radius=1 StartAngle=5.35e-14 EndAngle=1.5708
    g7: LineSegment StartX=10.0875 StartY=-1.11588 StartZ=0 EndX=10.0875 EndY=1.38411 EndZ=0
    g8: ArcOfCircle CenterX=7.08745 CenterY=1.38411 CenterZ=0 NormalX=0 NormalY=0 NormalZ=1 AngleXU=0 Radius=3 StartAngle=3.57e-14 EndAngle=1.5708
    g9: ArcOfCircle CenterX=4.58745 CenterY=1.38412 CenterZ=0 NormalX=0 NormalY=0 NormalZ=1 AngleXU=0 Radius=1 StartAngle=1.57081 EndAngle=3.14159
    g10: LineSegment StartX=4.58744 StartY=2.38411 StartZ=0 EndX=7.08745 EndY=2.38411 EndZ=0
    g11: LineSegment StartX=4.58745 StartY=4.38411 StartZ=0 EndX=7.08745 EndY=4.38411 EndZ=0
    g12: ArcOfCircle CenterX=4.58745 CenterY=5.38411 CenterZ=0 NormalX=0 NormalY=0 NormalZ=1 AngleXU=0 Radius=1 StartAngle=3.14159 EndAngle=4.71239
    g13: LineSegment StartX=3.58745 StartY=5.38411 StartZ=0 EndX=3.58745 EndY=1.38411 EndZ=0
  constraints (33):
    c: Vertical(g0)
    c: Block(g0)
    c: Block(g1)
    c: Coincident(g2,g1)
    c: Coincident(g3,g0)
    c: Coincident(g3,g2)
    c: Horizontal(g3)
    c: Block(g2)
    c: Coincident(g4,g0)
    c: Horizontal(g4)
    c: Coincident(g5,g2)
    c: Block(g5)
    c: Block(g4)
    c: Coincident(g6,g1)
    c: Block(g6)
    c: Coincident(g7,g5)
    c: Vertical(g7)
    c: Coincident(g8,g6)
    c: Block(g8)
    c: Block(g7)
    c: Coincident(g10,g9)
    c: Coincident(g10,g6)
    c: Horizontal(g10)
    c: Block(g10)
    c: Block(g9)
    c: Coincident(g11,g8)
    c: Horizontal(g11)
    c: Block(g12)
    c: Block(g11)
    c: Coincident(g13,g12)
    c: Coincident(g13,g9)
    c: Vertical(g13)
    c: Tangent(g13,g9)
FEATURE [Part::Extrusion] Extrude041
  Base = -> Sketch049
  Dir = (1,0,0)
  DirMode = 2
  FaceMakerClass = Part::FaceMakerBullseye
  LengthFwd = 10
  LengthRev = 0
  Placement = pos=(-2,-22.615,14.6) rot=(0,0,1;3.14159rad)
  Solid = true
  Symmetric = false
FEATURE [Part::MultiFuse] Fusion023
  Shapes = -> [Extrude039,Extrude040,Extrude041,Cut014,Fusion015]
